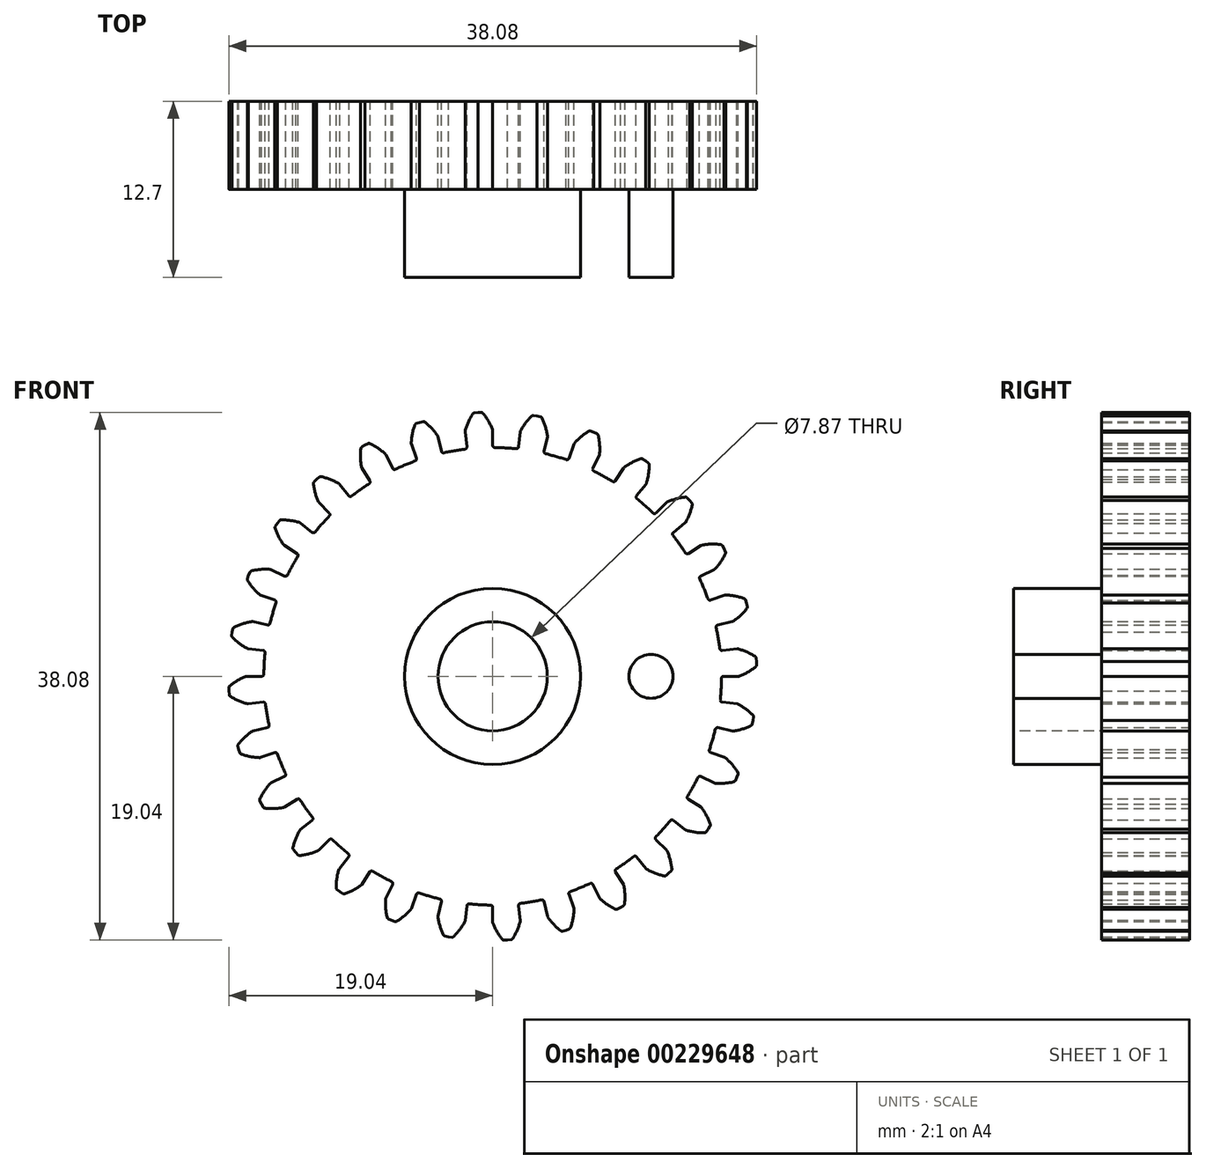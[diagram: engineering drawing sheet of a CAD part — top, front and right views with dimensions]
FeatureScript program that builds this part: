
annotation { "Feature Type Name" : "Feature", "Feature Type Description" : "" }
export const myFeature = defineFeature(function(context is Context, id is Id, definition is map)
    precondition{}
    {
        {
            var Q0;
            Q0=qCreatedBy(makeId("Front.planeOp"),FACE);
            var sketch = newSketch(context, id + "F0", { "sketchPlane" : qUnion([Q0])});
            skArc(sketch, "E0", {"start": v(-2, 16.39) * mm, "mid": v(-2.77, 16.28) * mm, "end": v(-3.53, 16.13) * mm});
            skArc(sketch, "E1.trimOffspring", {"start": v(-0.01, 17.8) * mm, "mid": v(-0.3, 18.42) * mm, "end": v(-0.7, 18.98) * mm});
            skLineSegment(sketch, "E2", {"start": v(-0.81, 19.04) * mm, "end": v(-1.07, 19.04) * mm});
            skLineSegment(sketch, "E3", {"start": v(0, 17.75) * mm, "end": v(0, 16.66) * mm});
            skLineSegment(sketch, "E4.MirrorCS", {"start": v(-1.33, 19) * mm, "end": v(-1.07, 19.04) * mm});
            skArc(sketch, "E5.MirrorCS", {"start": v(-1.98, 17.7) * mm, "mid": v(-1.76, 18.34) * mm, "end": v(-1.44, 18.94) * mm});
            skLineSegment(sketch, "E6.MirrorCS", {"start": v(-1.99, 17.64) * mm, "end": v(-1.87, 16.56) * mm});
            skPoint(sketch, "E7.orphan", {"position": v(0, 16.2) * mm});
            skPoint(sketch, "E8.orphan", {"position": v(-1.81, 16.1) * mm});
            skPoint(sketch, "E9.visualSharp", {"position": v(-1.85, 16.4) * mm});
            skArc(sketch, "E9.filletArc", {"start": v(-2, 16.39) * mm, "mid": v(-1.9, 16.45) * mm, "end": v(-1.87, 16.56) * mm});
            skPoint(sketch, "E10.visualSharp", {"position": v(0, 16.51) * mm});
            skArc(sketch, "E10.filletArc", {"start": v(0, 16.66) * mm, "mid": v(0.04, 16.55) * mm, "end": v(0.15, 16.5) * mm});
            skPoint(sketch, "E11.visualSharp", {"position": v(0, 17.78) * mm});
            skArc(sketch, "E11.filletArc", {"start": v(0, 17.75) * mm, "mid": v(0, 17.78) * mm, "end": v(-0.01, 17.8) * mm});
            skPoint(sketch, "E12.visualSharp", {"position": v(-0.74, 19.04) * mm});
            skArc(sketch, "E12.filletArc", {"start": v(-0.7, 18.98) * mm, "mid": v(-0.75, 19.02) * mm, "end": v(-0.81, 19.04) * mm});
            skPoint(sketch, "E13.visualSharp", {"position": v(-1.4, 19) * mm});
            skArc(sketch, "E13.filletArc", {"start": v(-1.33, 19) * mm, "mid": v(-1.39, 18.98) * mm, "end": v(-1.44, 18.94) * mm});
            skPoint(sketch, "E14.visualSharp", {"position": v(-2, 17.67) * mm});
            skArc(sketch, "E14.filletArc", {"start": v(-1.98, 17.7) * mm, "mid": v(-1.99, 17.67) * mm, "end": v(-1.99, 17.64) * mm});
            skArc(sketch, "E15.1.0", {"start": v(-3.97, 17.36) * mm, "mid": v(-4.4, 17.89) * mm, "end": v(-4.9, 18.35) * mm});
            skPoint(sketch, "E15.1.1", {"position": v(-5.59, 18.21) * mm});
            skPoint(sketch, "E15.1.2", {"position": v(-5.87, 16.78) * mm});
            skLineSegment(sketch, "E15.1.3", {"start": v(-3.95, 17.3) * mm, "end": v(-3.7, 16.24) * mm});
            skLineSegment(sketch, "E15.1.4", {"start": v(-5.86, 16.76) * mm, "end": v(-5.5, 15.73) * mm});
            skArc(sketch, "E15.1.5", {"start": v(-5.87, 16.81) * mm, "mid": v(-5.8, 17.49) * mm, "end": v(-5.62, 18.14) * mm});
            skPoint(sketch, "E15.1.6", {"position": v(-3.96, 17.33) * mm});
            skPoint(sketch, "E15.1.7", {"position": v(-4.96, 18.4) * mm});
            skLineSegment(sketch, "E15.1.8", {"start": v(-5.03, 18.38) * mm, "end": v(-5.28, 18.32) * mm});
            skLineSegment(sketch, "E15.1.9", {"start": v(-5.52, 18.24) * mm, "end": v(-5.28, 18.32) * mm});
            skArc(sketch, "E15.1.10", {"start": v(-5.87, 16.81) * mm, "mid": v(-5.87, 16.78) * mm, "end": v(-5.86, 16.76) * mm});
            skArc(sketch, "E15.1.11", {"start": v(-5.52, 18.24) * mm, "mid": v(-5.58, 18.2) * mm, "end": v(-5.62, 18.14) * mm});
            skArc(sketch, "E15.1.12", {"start": v(-4.9, 18.35) * mm, "mid": v(-4.96, 18.38) * mm, "end": v(-5.03, 18.38) * mm});
            skArc(sketch, "E15.1.13", {"start": v(-3.95, 17.3) * mm, "mid": v(-3.96, 17.33) * mm, "end": v(-3.97, 17.36) * mm});
            skArc(sketch, "E15.1.14", {"start": v(-5.6, 15.53) * mm, "mid": v(-5.5, 15.61) * mm, "end": v(-5.5, 15.73) * mm});
            skArc(sketch, "E15.1.15", {"start": v(-3.7, 16.24) * mm, "mid": v(-3.64, 16.15) * mm, "end": v(-3.53, 16.13) * mm});
            skArc(sketch, "E15.2.0", {"start": v(-7.74, 16.04) * mm, "mid": v(-8.27, 16.46) * mm, "end": v(-8.86, 16.8) * mm});
            skPoint(sketch, "E15.2.1", {"position": v(-9.5, 16.51) * mm});
            skPoint(sketch, "E15.2.2", {"position": v(-9.46, 15.05) * mm});
            skLineSegment(sketch, "E15.2.3", {"start": v(-7.7, 16) * mm, "end": v(-7.23, 15.01) * mm});
            skLineSegment(sketch, "E15.2.4", {"start": v(-9.44, 15.03) * mm, "end": v(-8.86, 14.1) * mm});
            skArc(sketch, "E15.2.5", {"start": v(-9.47, 15.08) * mm, "mid": v(-9.54, 15.76) * mm, "end": v(-9.51, 16.44) * mm});
            skPoint(sketch, "E15.2.6", {"position": v(-7.71, 16.02) * mm});
            skPoint(sketch, "E15.2.7", {"position": v(-8.92, 16.83) * mm});
            skLineSegment(sketch, "E15.2.8", {"start": v(-8.99, 16.8) * mm, "end": v(-9.22, 16.69) * mm});
            skLineSegment(sketch, "E15.2.9", {"start": v(-9.44, 16.55) * mm, "end": v(-9.22, 16.69) * mm});
            skArc(sketch, "E15.2.10", {"start": v(-9.47, 15.08) * mm, "mid": v(-9.46, 15.06) * mm, "end": v(-9.44, 15.03) * mm});
            skArc(sketch, "E15.2.11", {"start": v(-9.44, 16.55) * mm, "mid": v(-9.49, 16.5) * mm, "end": v(-9.51, 16.44) * mm});
            skArc(sketch, "E15.2.12", {"start": v(-8.86, 16.8) * mm, "mid": v(-8.92, 16.81) * mm, "end": v(-8.99, 16.8) * mm});
            skArc(sketch, "E15.2.13", {"start": v(-7.7, 16) * mm, "mid": v(-7.72, 16.02) * mm, "end": v(-7.74, 16.04) * mm});
            skArc(sketch, "E15.2.14", {"start": v(-8.91, 13.9) * mm, "mid": v(-8.84, 14) * mm, "end": v(-8.86, 14.1) * mm});
            skArc(sketch, "E15.2.15", {"start": v(-7.23, 15.01) * mm, "mid": v(-7.14, 14.93) * mm, "end": v(-7.03, 14.94) * mm});
            skArc(sketch, "E16.1.3.0", {"start": v(-11.11, 13.92) * mm, "mid": v(-11.72, 14.2) * mm, "end": v(-12.37, 14.4) * mm});
            skPoint(sketch, "E16.4.3.0", {"position": v(-12.94, 13.98) * mm});
            skPoint(sketch, "E16.5.3.0", {"position": v(-12.57, 12.57) * mm});
            skLineSegment(sketch, "E16.6.3.0", {"start": v(-11.07, 13.88) * mm, "end": v(-10.39, 13.03) * mm});
            skLineSegment(sketch, "E16.9.3.0", {"start": v(-12.55, 12.55) * mm, "end": v(-11.78, 11.78) * mm});
            skArc(sketch, "E16.12.3.0", {"start": v(-12.58, 12.6) * mm, "mid": v(-12.8, 13.24) * mm, "end": v(-12.93, 13.9) * mm});
            skPoint(sketch, "E16.16.3.0", {"position": v(-11.09, 13.9) * mm});
            skPoint(sketch, "E16.17.3.0", {"position": v(-12.45, 14.42) * mm});
            skLineSegment(sketch, "E16.18.3.0", {"start": v(-12.5, 14.38) * mm, "end": v(-12.7, 14.22) * mm});
            skLineSegment(sketch, "E16.21.3.0", {"start": v(-12.89, 14.03) * mm, "end": v(-12.7, 14.22) * mm});
            skArc(sketch, "E16.24.3.0", {"start": v(-12.58, 12.6) * mm, "mid": v(-12.57, 12.57) * mm, "end": v(-12.55, 12.55) * mm});
            skArc(sketch, "E16.28.3.0", {"start": v(-12.89, 14.03) * mm, "mid": v(-12.92, 13.98) * mm, "end": v(-12.93, 13.9) * mm});
            skArc(sketch, "E16.32.3.0", {"start": v(-12.37, 14.4) * mm, "mid": v(-12.44, 14.4) * mm, "end": v(-12.5, 14.38) * mm});
            skArc(sketch, "E16.36.3.0", {"start": v(-11.07, 13.88) * mm, "mid": v(-11.09, 13.9) * mm, "end": v(-11.11, 13.92) * mm});
            skArc(sketch, "E16.40.3.0", {"start": v(-11.78, 11.57) * mm, "mid": v(-11.74, 11.67) * mm, "end": v(-11.78, 11.78) * mm});
            skArc(sketch, "E16.44.3.0", {"start": v(-10.39, 13.03) * mm, "mid": v(-10.29, 12.97) * mm, "end": v(-10.18, 13) * mm});
            skArc(sketch, "E16.1.4.0", {"start": v(-13.93, 11.1) * mm, "mid": v(-14.6, 11.24) * mm, "end": v(-15.27, 11.3) * mm});
            skPoint(sketch, "E16.4.4.0", {"position": v(-15.72, 10.75) * mm});
            skPoint(sketch, "E16.5.4.0", {"position": v(-15.05, 9.46) * mm});
            skLineSegment(sketch, "E16.6.4.0", {"start": v(-13.88, 11.07) * mm, "end": v(-13.03, 10.39) * mm});
            skLineSegment(sketch, "E16.9.4.0", {"start": v(-15.03, 9.44) * mm, "end": v(-14.1, 8.86) * mm});
            skArc(sketch, "E16.12.4.0", {"start": v(-15.07, 9.48) * mm, "mid": v(-15.43, 10.06) * mm, "end": v(-15.7, 10.68) * mm});
            skPoint(sketch, "E16.16.4.0", {"position": v(-13.9, 11.09) * mm});
            skPoint(sketch, "E16.17.4.0", {"position": v(-15.34, 11.3) * mm});
            skLineSegment(sketch, "E16.18.4.0", {"start": v(-15.39, 11.23) * mm, "end": v(-15.55, 11.03) * mm});
            skLineSegment(sketch, "E16.21.4.0", {"start": v(-15.69, 10.81) * mm, "end": v(-15.55, 11.03) * mm});
            skArc(sketch, "E16.24.4.0", {"start": v(-15.07, 9.48) * mm, "mid": v(-15.05, 9.46) * mm, "end": v(-15.03, 9.44) * mm});
            skArc(sketch, "E16.28.4.0", {"start": v(-15.69, 10.81) * mm, "mid": v(-15.7, 10.75) * mm, "end": v(-15.7, 10.68) * mm});
            skArc(sketch, "E16.32.4.0", {"start": v(-15.27, 11.3) * mm, "mid": v(-15.34, 11.28) * mm, "end": v(-15.39, 11.23) * mm});
            skArc(sketch, "E16.36.4.0", {"start": v(-13.88, 11.07) * mm, "mid": v(-13.9, 11.08) * mm, "end": v(-13.93, 11.1) * mm});
            skArc(sketch, "E16.40.4.0", {"start": v(-14.06, 8.66) * mm, "mid": v(-14.04, 8.77) * mm, "end": v(-14.1, 8.86) * mm});
            skArc(sketch, "E16.44.4.0", {"start": v(-13.03, 10.39) * mm, "mid": v(-12.92, 10.36) * mm, "end": v(-12.81, 10.41) * mm});
            skArc(sketch, "E16.1.5.0", {"start": v(-16.05, 7.72) * mm, "mid": v(-16.73, 7.72) * mm, "end": v(-17.4, 7.61) * mm});
            skPoint(sketch, "E16.4.5.0", {"position": v(-17.72, 6.98) * mm});
            skPoint(sketch, "E16.5.5.0", {"position": v(-16.78, 5.87) * mm});
            skLineSegment(sketch, "E16.6.5.0", {"start": v(-16, 7.7) * mm, "end": v(-15.01, 7.23) * mm});
            skLineSegment(sketch, "E16.9.5.0", {"start": v(-16.76, 5.86) * mm, "end": v(-15.73, 5.5) * mm});
            skArc(sketch, "E16.12.5.0", {"start": v(-16.8, 5.9) * mm, "mid": v(-17.28, 6.37) * mm, "end": v(-17.69, 6.92) * mm});
            skPoint(sketch, "E16.16.5.0", {"position": v(-16.02, 7.71) * mm});
            skPoint(sketch, "E16.17.5.0", {"position": v(-17.47, 7.6) * mm});
            skLineSegment(sketch, "E16.18.5.0", {"start": v(-17.5, 7.53) * mm, "end": v(-17.61, 7.3) * mm});
            skLineSegment(sketch, "E16.21.5.0", {"start": v(-17.7, 7.05) * mm, "end": v(-17.61, 7.3) * mm});
            skArc(sketch, "E16.24.5.0", {"start": v(-16.8, 5.9) * mm, "mid": v(-16.78, 5.87) * mm, "end": v(-16.76, 5.86) * mm});
            skArc(sketch, "E16.28.5.0", {"start": v(-17.7, 7.05) * mm, "mid": v(-17.7, 6.99) * mm, "end": v(-17.69, 6.92) * mm});
            skArc(sketch, "E16.32.5.0", {"start": v(-17.4, 7.61) * mm, "mid": v(-17.46, 7.58) * mm, "end": v(-17.5, 7.53) * mm});
            skArc(sketch, "E16.36.5.0", {"start": v(-16, 7.7) * mm, "mid": v(-16.02, 7.71) * mm, "end": v(-16.05, 7.72) * mm});
            skArc(sketch, "E16.40.5.0", {"start": v(-15.63, 5.31) * mm, "mid": v(-15.64, 5.43) * mm, "end": v(-15.73, 5.5) * mm});
            skArc(sketch, "E16.44.5.0", {"start": v(-15.01, 7.23) * mm, "mid": v(-14.9, 7.22) * mm, "end": v(-14.8, 7.3) * mm});
            skArc(sketch, "E16.1.6.0", {"start": v(-17.36, 3.95) * mm, "mid": v(-18.03, 3.8) * mm, "end": v(-18.66, 3.55) * mm});
            skPoint(sketch, "E16.4.6.0", {"position": v(-18.83, 2.87) * mm});
            skPoint(sketch, "E16.5.6.0", {"position": v(-17.67, 2) * mm});
            skLineSegment(sketch, "E16.6.6.0", {"start": v(-17.3, 3.95) * mm, "end": v(-16.24, 3.7) * mm});
            skLineSegment(sketch, "E16.9.6.0", {"start": v(-17.64, 1.99) * mm, "end": v(-16.56, 1.87) * mm});
            skArc(sketch, "E16.12.6.0", {"start": v(-17.7, 2) * mm, "mid": v(-18.27, 2.37) * mm, "end": v(-18.78, 2.81) * mm});
            skPoint(sketch, "E16.16.6.0", {"position": v(-17.33, 3.96) * mm});
            skPoint(sketch, "E16.17.6.0", {"position": v(-18.72, 3.52) * mm});
            skLineSegment(sketch, "E16.18.6.0", {"start": v(-18.74, 3.45) * mm, "end": v(-18.8, 3.2) * mm});
            skLineSegment(sketch, "E16.21.6.0", {"start": v(-18.83, 2.94) * mm, "end": v(-18.8, 3.2) * mm});
            skArc(sketch, "E16.24.6.0", {"start": v(-17.7, 2) * mm, "mid": v(-17.67, 2) * mm, "end": v(-17.64, 1.99) * mm});
            skArc(sketch, "E16.28.6.0", {"start": v(-18.83, 2.94) * mm, "mid": v(-18.82, 2.87) * mm, "end": v(-18.78, 2.81) * mm});
            skArc(sketch, "E16.32.6.0", {"start": v(-18.66, 3.55) * mm, "mid": v(-18.7, 3.5) * mm, "end": v(-18.74, 3.45) * mm});
            skArc(sketch, "E16.36.6.0", {"start": v(-17.3, 3.95) * mm, "mid": v(-17.33, 3.95) * mm, "end": v(-17.36, 3.95) * mm});
            skArc(sketch, "E16.40.6.0", {"start": v(-16.42, 1.7) * mm, "mid": v(-16.46, 1.8) * mm, "end": v(-16.56, 1.87) * mm});
            skArc(sketch, "E16.44.6.0", {"start": v(-16.24, 3.7) * mm, "mid": v(-16.13, 3.73) * mm, "end": v(-16.06, 3.82) * mm});
            skArc(sketch, "E16.1.7.0", {"start": v(-17.8, -0.01) * mm, "mid": v(-18.42, -0.3) * mm, "end": v(-18.98, -0.7) * mm});
            skPoint(sketch, "E16.4.7.0", {"position": v(-19, -1.4) * mm});
            skPoint(sketch, "E16.5.7.0", {"position": v(-17.67, -2) * mm});
            skLineSegment(sketch, "E16.6.7.0", {"start": v(-17.75, 0) * mm, "end": v(-16.66, 0) * mm});
            skLineSegment(sketch, "E16.9.7.0", {"start": v(-17.64, -1.99) * mm, "end": v(-16.56, -1.87) * mm});
            skArc(sketch, "E16.12.7.0", {"start": v(-17.7, -1.98) * mm, "mid": v(-18.34, -1.76) * mm, "end": v(-18.94, -1.44) * mm});
            skPoint(sketch, "E16.16.7.0", {"position": v(-17.78, 0) * mm});
            skPoint(sketch, "E16.17.7.0", {"position": v(-19.04, -0.74) * mm});
            skLineSegment(sketch, "E16.18.7.0", {"start": v(-19.04, -0.81) * mm, "end": v(-19.04, -1.07) * mm});
            skLineSegment(sketch, "E16.21.7.0", {"start": v(-19, -1.33) * mm, "end": v(-19.04, -1.07) * mm});
            skArc(sketch, "E16.24.7.0", {"start": v(-17.7, -1.98) * mm, "mid": v(-17.67, -1.99) * mm, "end": v(-17.64, -1.99) * mm});
            skArc(sketch, "E16.28.7.0", {"start": v(-19, -1.33) * mm, "mid": v(-18.98, -1.39) * mm, "end": v(-18.94, -1.44) * mm});
            skArc(sketch, "E16.32.7.0", {"start": v(-18.98, -0.7) * mm, "mid": v(-19.02, -0.75) * mm, "end": v(-19.04, -0.81) * mm});
            skArc(sketch, "E16.36.7.0", {"start": v(-17.75, 0) * mm, "mid": v(-17.78, 0) * mm, "end": v(-17.8, -0.01) * mm});
            skArc(sketch, "E16.40.7.0", {"start": v(-16.39, -2) * mm, "mid": v(-16.45, -1.9) * mm, "end": v(-16.56, -1.87) * mm});
            skArc(sketch, "E16.44.7.0", {"start": v(-16.66, 0) * mm, "mid": v(-16.55, 0.04) * mm, "end": v(-16.5, 0.15) * mm});
            skArc(sketch, "E16.1.8.0", {"start": v(-17.36, -3.97) * mm, "mid": v(-17.89, -4.4) * mm, "end": v(-18.35, -4.9) * mm});
            skPoint(sketch, "E16.4.8.0", {"position": v(-18.21, -5.59) * mm});
            skPoint(sketch, "E16.5.8.0", {"position": v(-16.78, -5.87) * mm});
            skLineSegment(sketch, "E16.6.8.0", {"start": v(-17.3, -3.95) * mm, "end": v(-16.24, -3.7) * mm});
            skLineSegment(sketch, "E16.9.8.0", {"start": v(-16.76, -5.86) * mm, "end": v(-15.73, -5.5) * mm});
            skArc(sketch, "E16.12.8.0", {"start": v(-16.81, -5.87) * mm, "mid": v(-17.49, -5.8) * mm, "end": v(-18.14, -5.62) * mm});
            skPoint(sketch, "E16.16.8.0", {"position": v(-17.33, -3.96) * mm});
            skPoint(sketch, "E16.17.8.0", {"position": v(-18.4, -4.96) * mm});
            skLineSegment(sketch, "E16.18.8.0", {"start": v(-18.38, -5.03) * mm, "end": v(-18.32, -5.28) * mm});
            skLineSegment(sketch, "E16.21.8.0", {"start": v(-18.24, -5.52) * mm, "end": v(-18.32, -5.28) * mm});
            skArc(sketch, "E16.24.8.0", {"start": v(-16.81, -5.87) * mm, "mid": v(-16.78, -5.87) * mm, "end": v(-16.76, -5.86) * mm});
            skArc(sketch, "E16.28.8.0", {"start": v(-18.24, -5.52) * mm, "mid": v(-18.2, -5.58) * mm, "end": v(-18.14, -5.62) * mm});
            skArc(sketch, "E16.32.8.0", {"start": v(-18.35, -4.9) * mm, "mid": v(-18.38, -4.96) * mm, "end": v(-18.38, -5.03) * mm});
            skArc(sketch, "E16.36.8.0", {"start": v(-17.3, -3.95) * mm, "mid": v(-17.33, -3.96) * mm, "end": v(-17.36, -3.97) * mm});
            skArc(sketch, "E16.40.8.0", {"start": v(-15.53, -5.6) * mm, "mid": v(-15.61, -5.5) * mm, "end": v(-15.73, -5.5) * mm});
            skArc(sketch, "E16.44.8.0", {"start": v(-16.24, -3.7) * mm, "mid": v(-16.15, -3.64) * mm, "end": v(-16.13, -3.53) * mm});
            skArc(sketch, "E16.1.9.0", {"start": v(-16.04, -7.74) * mm, "mid": v(-16.46, -8.27) * mm, "end": v(-16.8, -8.86) * mm});
            skPoint(sketch, "E16.4.9.0", {"position": v(-16.51, -9.5) * mm});
            skPoint(sketch, "E16.5.9.0", {"position": v(-15.05, -9.46) * mm});
            skLineSegment(sketch, "E16.6.9.0", {"start": v(-16, -7.7) * mm, "end": v(-15.01, -7.23) * mm});
            skLineSegment(sketch, "E16.9.9.0", {"start": v(-15.03, -9.44) * mm, "end": v(-14.1, -8.86) * mm});
            skArc(sketch, "E16.12.9.0", {"start": v(-15.08, -9.47) * mm, "mid": v(-15.76, -9.54) * mm, "end": v(-16.44, -9.51) * mm});
            skPoint(sketch, "E16.16.9.0", {"position": v(-16.02, -7.71) * mm});
            skPoint(sketch, "E16.17.9.0", {"position": v(-16.83, -8.92) * mm});
            skLineSegment(sketch, "E16.18.9.0", {"start": v(-16.8, -8.99) * mm, "end": v(-16.69, -9.22) * mm});
            skLineSegment(sketch, "E16.21.9.0", {"start": v(-16.55, -9.44) * mm, "end": v(-16.69, -9.22) * mm});
            skArc(sketch, "E16.24.9.0", {"start": v(-15.08, -9.47) * mm, "mid": v(-15.06, -9.46) * mm, "end": v(-15.03, -9.44) * mm});
            skArc(sketch, "E16.28.9.0", {"start": v(-16.55, -9.44) * mm, "mid": v(-16.5, -9.49) * mm, "end": v(-16.44, -9.51) * mm});
            skArc(sketch, "E16.32.9.0", {"start": v(-16.8, -8.86) * mm, "mid": v(-16.81, -8.92) * mm, "end": v(-16.8, -8.99) * mm});
            skArc(sketch, "E16.36.9.0", {"start": v(-16, -7.7) * mm, "mid": v(-16.02, -7.72) * mm, "end": v(-16.04, -7.74) * mm});
            skArc(sketch, "E16.40.9.0", {"start": v(-13.9, -8.91) * mm, "mid": v(-14, -8.84) * mm, "end": v(-14.1, -8.86) * mm});
            skArc(sketch, "E16.44.9.0", {"start": v(-15.01, -7.23) * mm, "mid": v(-14.93, -7.14) * mm, "end": v(-14.94, -7.03) * mm});
            skArc(sketch, "E16.1.10.0", {"start": v(-13.92, -11.11) * mm, "mid": v(-14.2, -11.72) * mm, "end": v(-14.4, -12.37) * mm});
            skPoint(sketch, "E16.4.10.0", {"position": v(-13.98, -12.94) * mm});
            skPoint(sketch, "E16.5.10.0", {"position": v(-12.57, -12.57) * mm});
            skLineSegment(sketch, "E16.6.10.0", {"start": v(-13.88, -11.07) * mm, "end": v(-13.03, -10.39) * mm});
            skLineSegment(sketch, "E16.9.10.0", {"start": v(-12.55, -12.55) * mm, "end": v(-11.78, -11.78) * mm});
            skArc(sketch, "E16.12.10.0", {"start": v(-12.6, -12.58) * mm, "mid": v(-13.24, -12.8) * mm, "end": v(-13.9, -12.93) * mm});
            skPoint(sketch, "E16.16.10.0", {"position": v(-13.9, -11.09) * mm});
            skPoint(sketch, "E16.17.10.0", {"position": v(-14.42, -12.45) * mm});
            skLineSegment(sketch, "E16.18.10.0", {"start": v(-14.38, -12.5) * mm, "end": v(-14.22, -12.7) * mm});
            skLineSegment(sketch, "E16.21.10.0", {"start": v(-14.03, -12.89) * mm, "end": v(-14.22, -12.7) * mm});
            skArc(sketch, "E16.24.10.0", {"start": v(-12.6, -12.58) * mm, "mid": v(-12.57, -12.57) * mm, "end": v(-12.55, -12.55) * mm});
            skArc(sketch, "E16.28.10.0", {"start": v(-14.03, -12.89) * mm, "mid": v(-13.98, -12.92) * mm, "end": v(-13.9, -12.93) * mm});
            skArc(sketch, "E16.32.10.0", {"start": v(-14.4, -12.37) * mm, "mid": v(-14.4, -12.44) * mm, "end": v(-14.38, -12.5) * mm});
            skArc(sketch, "E16.36.10.0", {"start": v(-13.88, -11.07) * mm, "mid": v(-13.9, -11.09) * mm, "end": v(-13.92, -11.11) * mm});
            skArc(sketch, "E16.40.10.0", {"start": v(-11.57, -11.78) * mm, "mid": v(-11.67, -11.74) * mm, "end": v(-11.78, -11.78) * mm});
            skArc(sketch, "E16.44.10.0", {"start": v(-13.03, -10.39) * mm, "mid": v(-12.97, -10.29) * mm, "end": v(-13, -10.18) * mm});
            skArc(sketch, "E16.1.11.0", {"start": v(-11.1, -13.93) * mm, "mid": v(-11.24, -14.6) * mm, "end": v(-11.3, -15.27) * mm});
            skPoint(sketch, "E16.4.11.0", {"position": v(-10.75, -15.72) * mm});
            skPoint(sketch, "E16.5.11.0", {"position": v(-9.46, -15.05) * mm});
            skLineSegment(sketch, "E16.6.11.0", {"start": v(-11.07, -13.88) * mm, "end": v(-10.39, -13.03) * mm});
            skLineSegment(sketch, "E16.9.11.0", {"start": v(-9.44, -15.03) * mm, "end": v(-8.86, -14.1) * mm});
            skArc(sketch, "E16.12.11.0", {"start": v(-9.48, -15.07) * mm, "mid": v(-10.06, -15.43) * mm, "end": v(-10.68, -15.7) * mm});
            skPoint(sketch, "E16.16.11.0", {"position": v(-11.09, -13.9) * mm});
            skPoint(sketch, "E16.17.11.0", {"position": v(-11.3, -15.34) * mm});
            skLineSegment(sketch, "E16.18.11.0", {"start": v(-11.23, -15.39) * mm, "end": v(-11.03, -15.55) * mm});
            skLineSegment(sketch, "E16.21.11.0", {"start": v(-10.81, -15.69) * mm, "end": v(-11.03, -15.55) * mm});
            skArc(sketch, "E16.24.11.0", {"start": v(-9.48, -15.07) * mm, "mid": v(-9.46, -15.05) * mm, "end": v(-9.44, -15.03) * mm});
            skArc(sketch, "E16.28.11.0", {"start": v(-10.81, -15.69) * mm, "mid": v(-10.75, -15.7) * mm, "end": v(-10.68, -15.7) * mm});
            skArc(sketch, "E16.32.11.0", {"start": v(-11.3, -15.27) * mm, "mid": v(-11.28, -15.34) * mm, "end": v(-11.23, -15.39) * mm});
            skArc(sketch, "E16.36.11.0", {"start": v(-11.07, -13.88) * mm, "mid": v(-11.08, -13.9) * mm, "end": v(-11.1, -13.93) * mm});
            skArc(sketch, "E16.40.11.0", {"start": v(-8.66, -14.06) * mm, "mid": v(-8.77, -14.04) * mm, "end": v(-8.86, -14.1) * mm});
            skArc(sketch, "E16.44.11.0", {"start": v(-10.39, -13.03) * mm, "mid": v(-10.36, -12.92) * mm, "end": v(-10.41, -12.81) * mm});
            skArc(sketch, "E16.1.12.0", {"start": v(-7.72, -16.05) * mm, "mid": v(-7.72, -16.73) * mm, "end": v(-7.61, -17.4) * mm});
            skPoint(sketch, "E16.4.12.0", {"position": v(-6.98, -17.72) * mm});
            skPoint(sketch, "E16.5.12.0", {"position": v(-5.87, -16.78) * mm});
            skLineSegment(sketch, "E16.6.12.0", {"start": v(-7.7, -16) * mm, "end": v(-7.23, -15.01) * mm});
            skLineSegment(sketch, "E16.9.12.0", {"start": v(-5.86, -16.76) * mm, "end": v(-5.5, -15.73) * mm});
            skArc(sketch, "E16.12.12.0", {"start": v(-5.9, -16.8) * mm, "mid": v(-6.37, -17.28) * mm, "end": v(-6.92, -17.69) * mm});
            skPoint(sketch, "E16.16.12.0", {"position": v(-7.71, -16.02) * mm});
            skPoint(sketch, "E16.17.12.0", {"position": v(-7.6, -17.47) * mm});
            skLineSegment(sketch, "E16.18.12.0", {"start": v(-7.53, -17.5) * mm, "end": v(-7.3, -17.61) * mm});
            skLineSegment(sketch, "E16.21.12.0", {"start": v(-7.05, -17.7) * mm, "end": v(-7.3, -17.61) * mm});
            skArc(sketch, "E16.24.12.0", {"start": v(-5.9, -16.8) * mm, "mid": v(-5.87, -16.78) * mm, "end": v(-5.86, -16.76) * mm});
            skArc(sketch, "E16.28.12.0", {"start": v(-7.05, -17.7) * mm, "mid": v(-6.99, -17.7) * mm, "end": v(-6.92, -17.69) * mm});
            skArc(sketch, "E16.32.12.0", {"start": v(-7.61, -17.4) * mm, "mid": v(-7.58, -17.46) * mm, "end": v(-7.53, -17.5) * mm});
            skArc(sketch, "E16.36.12.0", {"start": v(-7.7, -16) * mm, "mid": v(-7.71, -16.02) * mm, "end": v(-7.72, -16.05) * mm});
            skArc(sketch, "E16.40.12.0", {"start": v(-5.31, -15.63) * mm, "mid": v(-5.43, -15.64) * mm, "end": v(-5.5, -15.73) * mm});
            skArc(sketch, "E16.44.12.0", {"start": v(-7.23, -15.01) * mm, "mid": v(-7.22, -14.9) * mm, "end": v(-7.3, -14.8) * mm});
            skArc(sketch, "E16.1.13.0", {"start": v(-3.95, -17.36) * mm, "mid": v(-3.8, -18.03) * mm, "end": v(-3.55, -18.66) * mm});
            skPoint(sketch, "E16.4.13.0", {"position": v(-2.87, -18.83) * mm});
            skPoint(sketch, "E16.5.13.0", {"position": v(-2, -17.67) * mm});
            skLineSegment(sketch, "E16.6.13.0", {"start": v(-3.95, -17.3) * mm, "end": v(-3.7, -16.24) * mm});
            skLineSegment(sketch, "E16.9.13.0", {"start": v(-1.99, -17.64) * mm, "end": v(-1.87, -16.56) * mm});
            skArc(sketch, "E16.12.13.0", {"start": v(-2, -17.7) * mm, "mid": v(-2.37, -18.27) * mm, "end": v(-2.81, -18.78) * mm});
            skPoint(sketch, "E16.16.13.0", {"position": v(-3.96, -17.33) * mm});
            skPoint(sketch, "E16.17.13.0", {"position": v(-3.52, -18.72) * mm});
            skLineSegment(sketch, "E16.18.13.0", {"start": v(-3.45, -18.74) * mm, "end": v(-3.2, -18.8) * mm});
            skLineSegment(sketch, "E16.21.13.0", {"start": v(-2.94, -18.83) * mm, "end": v(-3.2, -18.8) * mm});
            skArc(sketch, "E16.24.13.0", {"start": v(-2, -17.7) * mm, "mid": v(-2, -17.67) * mm, "end": v(-1.99, -17.64) * mm});
            skArc(sketch, "E16.28.13.0", {"start": v(-2.94, -18.83) * mm, "mid": v(-2.87, -18.82) * mm, "end": v(-2.81, -18.78) * mm});
            skArc(sketch, "E16.32.13.0", {"start": v(-3.55, -18.66) * mm, "mid": v(-3.5, -18.7) * mm, "end": v(-3.45, -18.74) * mm});
            skArc(sketch, "E16.36.13.0", {"start": v(-3.95, -17.3) * mm, "mid": v(-3.95, -17.33) * mm, "end": v(-3.95, -17.36) * mm});
            skArc(sketch, "E16.40.13.0", {"start": v(-1.7, -16.42) * mm, "mid": v(-1.8, -16.46) * mm, "end": v(-1.87, -16.56) * mm});
            skArc(sketch, "E16.44.13.0", {"start": v(-3.7, -16.24) * mm, "mid": v(-3.73, -16.13) * mm, "end": v(-3.82, -16.06) * mm});
            skArc(sketch, "E16.1.14.0", {"start": v(0.01, -17.8) * mm, "mid": v(0.3, -18.42) * mm, "end": v(0.7, -18.98) * mm});
            skPoint(sketch, "E16.4.14.0", {"position": v(1.4, -19) * mm});
            skPoint(sketch, "E16.5.14.0", {"position": v(2, -17.67) * mm});
            skLineSegment(sketch, "E16.6.14.0", {"start": v(0, -17.75) * mm, "end": v(0, -16.66) * mm});
            skLineSegment(sketch, "E16.9.14.0", {"start": v(1.99, -17.64) * mm, "end": v(1.87, -16.56) * mm});
            skArc(sketch, "E16.12.14.0", {"start": v(1.98, -17.7) * mm, "mid": v(1.76, -18.34) * mm, "end": v(1.44, -18.94) * mm});
            skPoint(sketch, "E16.16.14.0", {"position": v(0, -17.78) * mm});
            skPoint(sketch, "E16.17.14.0", {"position": v(0.74, -19.04) * mm});
            skLineSegment(sketch, "E16.18.14.0", {"start": v(0.81, -19.04) * mm, "end": v(1.07, -19.04) * mm});
            skLineSegment(sketch, "E16.21.14.0", {"start": v(1.33, -19) * mm, "end": v(1.07, -19.04) * mm});
            skArc(sketch, "E16.24.14.0", {"start": v(1.98, -17.7) * mm, "mid": v(1.99, -17.67) * mm, "end": v(1.99, -17.64) * mm});
            skArc(sketch, "E16.28.14.0", {"start": v(1.33, -19) * mm, "mid": v(1.39, -18.98) * mm, "end": v(1.44, -18.94) * mm});
            skArc(sketch, "E16.32.14.0", {"start": v(0.7, -18.98) * mm, "mid": v(0.75, -19.02) * mm, "end": v(0.81, -19.04) * mm});
            skArc(sketch, "E16.36.14.0", {"start": v(0, -17.75) * mm, "mid": v(0, -17.78) * mm, "end": v(0.01, -17.8) * mm});
            skArc(sketch, "E16.40.14.0", {"start": v(2, -16.39) * mm, "mid": v(1.9, -16.45) * mm, "end": v(1.87, -16.56) * mm});
            skArc(sketch, "E16.44.14.0", {"start": v(0, -16.66) * mm, "mid": v(-0.04, -16.55) * mm, "end": v(-0.15, -16.5) * mm});
            skArc(sketch, "E16.1.15.0", {"start": v(3.97, -17.36) * mm, "mid": v(4.4, -17.89) * mm, "end": v(4.9, -18.35) * mm});
            skPoint(sketch, "E16.4.15.0", {"position": v(5.59, -18.21) * mm});
            skPoint(sketch, "E16.5.15.0", {"position": v(5.87, -16.78) * mm});
            skLineSegment(sketch, "E16.6.15.0", {"start": v(3.95, -17.3) * mm, "end": v(3.7, -16.24) * mm});
            skLineSegment(sketch, "E16.9.15.0", {"start": v(5.86, -16.76) * mm, "end": v(5.5, -15.73) * mm});
            skArc(sketch, "E16.12.15.0", {"start": v(5.87, -16.81) * mm, "mid": v(5.8, -17.49) * mm, "end": v(5.62, -18.14) * mm});
            skPoint(sketch, "E16.16.15.0", {"position": v(3.96, -17.33) * mm});
            skPoint(sketch, "E16.17.15.0", {"position": v(4.96, -18.4) * mm});
            skLineSegment(sketch, "E16.18.15.0", {"start": v(5.03, -18.38) * mm, "end": v(5.28, -18.32) * mm});
            skLineSegment(sketch, "E16.21.15.0", {"start": v(5.52, -18.24) * mm, "end": v(5.28, -18.32) * mm});
            skArc(sketch, "E16.24.15.0", {"start": v(5.87, -16.81) * mm, "mid": v(5.87, -16.78) * mm, "end": v(5.86, -16.76) * mm});
            skArc(sketch, "E16.28.15.0", {"start": v(5.52, -18.24) * mm, "mid": v(5.58, -18.2) * mm, "end": v(5.62, -18.14) * mm});
            skArc(sketch, "E16.32.15.0", {"start": v(4.9, -18.35) * mm, "mid": v(4.96, -18.38) * mm, "end": v(5.03, -18.38) * mm});
            skArc(sketch, "E16.36.15.0", {"start": v(3.95, -17.3) * mm, "mid": v(3.96, -17.33) * mm, "end": v(3.97, -17.36) * mm});
            skArc(sketch, "E16.40.15.0", {"start": v(5.6, -15.53) * mm, "mid": v(5.5, -15.61) * mm, "end": v(5.5, -15.73) * mm});
            skArc(sketch, "E16.44.15.0", {"start": v(3.7, -16.24) * mm, "mid": v(3.64, -16.15) * mm, "end": v(3.53, -16.13) * mm});
            skArc(sketch, "E16.1.16.0", {"start": v(7.74, -16.04) * mm, "mid": v(8.27, -16.46) * mm, "end": v(8.86, -16.8) * mm});
            skPoint(sketch, "E16.4.16.0", {"position": v(9.5, -16.51) * mm});
            skPoint(sketch, "E16.5.16.0", {"position": v(9.46, -15.05) * mm});
            skLineSegment(sketch, "E16.6.16.0", {"start": v(7.7, -16) * mm, "end": v(7.23, -15.01) * mm});
            skLineSegment(sketch, "E16.9.16.0", {"start": v(9.44, -15.03) * mm, "end": v(8.86, -14.1) * mm});
            skArc(sketch, "E16.12.16.0", {"start": v(9.47, -15.08) * mm, "mid": v(9.54, -15.76) * mm, "end": v(9.51, -16.44) * mm});
            skPoint(sketch, "E16.16.16.0", {"position": v(7.71, -16.02) * mm});
            skPoint(sketch, "E16.17.16.0", {"position": v(8.92, -16.83) * mm});
            skLineSegment(sketch, "E16.18.16.0", {"start": v(8.99, -16.8) * mm, "end": v(9.22, -16.69) * mm});
            skLineSegment(sketch, "E16.21.16.0", {"start": v(9.44, -16.55) * mm, "end": v(9.22, -16.69) * mm});
            skArc(sketch, "E16.24.16.0", {"start": v(9.47, -15.08) * mm, "mid": v(9.46, -15.06) * mm, "end": v(9.44, -15.03) * mm});
            skArc(sketch, "E16.28.16.0", {"start": v(9.44, -16.55) * mm, "mid": v(9.49, -16.5) * mm, "end": v(9.51, -16.44) * mm});
            skArc(sketch, "E16.32.16.0", {"start": v(8.86, -16.8) * mm, "mid": v(8.92, -16.81) * mm, "end": v(8.99, -16.8) * mm});
            skArc(sketch, "E16.36.16.0", {"start": v(7.7, -16) * mm, "mid": v(7.72, -16.02) * mm, "end": v(7.74, -16.04) * mm});
            skArc(sketch, "E16.40.16.0", {"start": v(8.91, -13.9) * mm, "mid": v(8.84, -14) * mm, "end": v(8.86, -14.1) * mm});
            skArc(sketch, "E16.44.16.0", {"start": v(7.23, -15.01) * mm, "mid": v(7.14, -14.93) * mm, "end": v(7.03, -14.94) * mm});
            skArc(sketch, "E16.1.17.0", {"start": v(11.11, -13.92) * mm, "mid": v(11.72, -14.2) * mm, "end": v(12.37, -14.4) * mm});
            skPoint(sketch, "E16.4.17.0", {"position": v(12.94, -13.98) * mm});
            skPoint(sketch, "E16.5.17.0", {"position": v(12.57, -12.57) * mm});
            skLineSegment(sketch, "E16.6.17.0", {"start": v(11.07, -13.88) * mm, "end": v(10.39, -13.03) * mm});
            skLineSegment(sketch, "E16.9.17.0", {"start": v(12.55, -12.55) * mm, "end": v(11.78, -11.78) * mm});
            skArc(sketch, "E16.12.17.0", {"start": v(12.58, -12.6) * mm, "mid": v(12.8, -13.24) * mm, "end": v(12.93, -13.9) * mm});
            skPoint(sketch, "E16.16.17.0", {"position": v(11.09, -13.9) * mm});
            skPoint(sketch, "E16.17.17.0", {"position": v(12.45, -14.42) * mm});
            skLineSegment(sketch, "E16.18.17.0", {"start": v(12.5, -14.38) * mm, "end": v(12.7, -14.22) * mm});
            skLineSegment(sketch, "E16.21.17.0", {"start": v(12.89, -14.03) * mm, "end": v(12.7, -14.22) * mm});
            skArc(sketch, "E16.24.17.0", {"start": v(12.58, -12.6) * mm, "mid": v(12.57, -12.57) * mm, "end": v(12.55, -12.55) * mm});
            skArc(sketch, "E16.28.17.0", {"start": v(12.89, -14.03) * mm, "mid": v(12.92, -13.98) * mm, "end": v(12.93, -13.9) * mm});
            skArc(sketch, "E16.32.17.0", {"start": v(12.37, -14.4) * mm, "mid": v(12.44, -14.4) * mm, "end": v(12.5, -14.38) * mm});
            skArc(sketch, "E16.36.17.0", {"start": v(11.07, -13.88) * mm, "mid": v(11.09, -13.9) * mm, "end": v(11.11, -13.92) * mm});
            skArc(sketch, "E16.40.17.0", {"start": v(11.78, -11.57) * mm, "mid": v(11.74, -11.67) * mm, "end": v(11.78, -11.78) * mm});
            skArc(sketch, "E16.44.17.0", {"start": v(10.39, -13.03) * mm, "mid": v(10.29, -12.97) * mm, "end": v(10.18, -13) * mm});
            skArc(sketch, "E16.1.18.0", {"start": v(13.93, -11.1) * mm, "mid": v(14.6, -11.24) * mm, "end": v(15.27, -11.3) * mm});
            skPoint(sketch, "E16.4.18.0", {"position": v(15.72, -10.75) * mm});
            skPoint(sketch, "E16.5.18.0", {"position": v(15.05, -9.46) * mm});
            skLineSegment(sketch, "E16.6.18.0", {"start": v(13.88, -11.07) * mm, "end": v(13.03, -10.39) * mm});
            skLineSegment(sketch, "E16.9.18.0", {"start": v(15.03, -9.44) * mm, "end": v(14.1, -8.86) * mm});
            skArc(sketch, "E16.12.18.0", {"start": v(15.07, -9.48) * mm, "mid": v(15.43, -10.06) * mm, "end": v(15.7, -10.68) * mm});
            skPoint(sketch, "E16.16.18.0", {"position": v(13.9, -11.09) * mm});
            skPoint(sketch, "E16.17.18.0", {"position": v(15.34, -11.3) * mm});
            skLineSegment(sketch, "E16.18.18.0", {"start": v(15.39, -11.23) * mm, "end": v(15.55, -11.03) * mm});
            skLineSegment(sketch, "E16.21.18.0", {"start": v(15.69, -10.81) * mm, "end": v(15.55, -11.03) * mm});
            skArc(sketch, "E16.24.18.0", {"start": v(15.07, -9.48) * mm, "mid": v(15.05, -9.46) * mm, "end": v(15.03, -9.44) * mm});
            skArc(sketch, "E16.28.18.0", {"start": v(15.69, -10.81) * mm, "mid": v(15.7, -10.75) * mm, "end": v(15.7, -10.68) * mm});
            skArc(sketch, "E16.32.18.0", {"start": v(15.27, -11.3) * mm, "mid": v(15.34, -11.28) * mm, "end": v(15.39, -11.23) * mm});
            skArc(sketch, "E16.36.18.0", {"start": v(13.88, -11.07) * mm, "mid": v(13.9, -11.08) * mm, "end": v(13.93, -11.1) * mm});
            skArc(sketch, "E16.40.18.0", {"start": v(14.06, -8.66) * mm, "mid": v(14.04, -8.77) * mm, "end": v(14.1, -8.86) * mm});
            skArc(sketch, "E16.44.18.0", {"start": v(13.03, -10.39) * mm, "mid": v(12.92, -10.36) * mm, "end": v(12.81, -10.41) * mm});
            skArc(sketch, "E16.1.19.0", {"start": v(16.05, -7.72) * mm, "mid": v(16.73, -7.72) * mm, "end": v(17.4, -7.61) * mm});
            skPoint(sketch, "E16.4.19.0", {"position": v(17.72, -6.98) * mm});
            skPoint(sketch, "E16.5.19.0", {"position": v(16.78, -5.87) * mm});
            skLineSegment(sketch, "E16.6.19.0", {"start": v(16, -7.7) * mm, "end": v(15.01, -7.23) * mm});
            skLineSegment(sketch, "E16.9.19.0", {"start": v(16.76, -5.86) * mm, "end": v(15.73, -5.5) * mm});
            skArc(sketch, "E16.12.19.0", {"start": v(16.8, -5.9) * mm, "mid": v(17.28, -6.37) * mm, "end": v(17.69, -6.92) * mm});
            skPoint(sketch, "E16.16.19.0", {"position": v(16.02, -7.71) * mm});
            skPoint(sketch, "E16.17.19.0", {"position": v(17.47, -7.6) * mm});
            skLineSegment(sketch, "E16.18.19.0", {"start": v(17.5, -7.53) * mm, "end": v(17.61, -7.3) * mm});
            skLineSegment(sketch, "E16.21.19.0", {"start": v(17.7, -7.05) * mm, "end": v(17.61, -7.3) * mm});
            skArc(sketch, "E16.24.19.0", {"start": v(16.8, -5.9) * mm, "mid": v(16.78, -5.87) * mm, "end": v(16.76, -5.86) * mm});
            skArc(sketch, "E16.28.19.0", {"start": v(17.7, -7.05) * mm, "mid": v(17.7, -6.99) * mm, "end": v(17.69, -6.92) * mm});
            skArc(sketch, "E16.32.19.0", {"start": v(17.4, -7.61) * mm, "mid": v(17.46, -7.58) * mm, "end": v(17.5, -7.53) * mm});
            skArc(sketch, "E16.36.19.0", {"start": v(16, -7.7) * mm, "mid": v(16.02, -7.71) * mm, "end": v(16.05, -7.72) * mm});
            skArc(sketch, "E16.40.19.0", {"start": v(15.63, -5.31) * mm, "mid": v(15.64, -5.43) * mm, "end": v(15.73, -5.5) * mm});
            skArc(sketch, "E16.44.19.0", {"start": v(15.01, -7.23) * mm, "mid": v(14.9, -7.22) * mm, "end": v(14.8, -7.3) * mm});
            skArc(sketch, "E16.1.20.0", {"start": v(17.36, -3.95) * mm, "mid": v(18.03, -3.8) * mm, "end": v(18.66, -3.55) * mm});
            skPoint(sketch, "E16.4.20.0", {"position": v(18.83, -2.87) * mm});
            skPoint(sketch, "E16.5.20.0", {"position": v(17.67, -2) * mm});
            skLineSegment(sketch, "E16.6.20.0", {"start": v(17.3, -3.95) * mm, "end": v(16.24, -3.7) * mm});
            skLineSegment(sketch, "E16.9.20.0", {"start": v(17.64, -1.99) * mm, "end": v(16.56, -1.87) * mm});
            skArc(sketch, "E16.12.20.0", {"start": v(17.7, -2) * mm, "mid": v(18.27, -2.37) * mm, "end": v(18.78, -2.81) * mm});
            skPoint(sketch, "E16.16.20.0", {"position": v(17.33, -3.96) * mm});
            skPoint(sketch, "E16.17.20.0", {"position": v(18.72, -3.52) * mm});
            skLineSegment(sketch, "E16.18.20.0", {"start": v(18.74, -3.45) * mm, "end": v(18.8, -3.2) * mm});
            skLineSegment(sketch, "E16.21.20.0", {"start": v(18.83, -2.94) * mm, "end": v(18.8, -3.2) * mm});
            skArc(sketch, "E16.24.20.0", {"start": v(17.7, -2) * mm, "mid": v(17.67, -2) * mm, "end": v(17.64, -1.99) * mm});
            skArc(sketch, "E16.28.20.0", {"start": v(18.83, -2.94) * mm, "mid": v(18.82, -2.87) * mm, "end": v(18.78, -2.81) * mm});
            skArc(sketch, "E16.32.20.0", {"start": v(18.66, -3.55) * mm, "mid": v(18.7, -3.5) * mm, "end": v(18.74, -3.45) * mm});
            skArc(sketch, "E16.36.20.0", {"start": v(17.3, -3.95) * mm, "mid": v(17.33, -3.95) * mm, "end": v(17.36, -3.95) * mm});
            skArc(sketch, "E16.40.20.0", {"start": v(16.42, -1.7) * mm, "mid": v(16.46, -1.8) * mm, "end": v(16.56, -1.87) * mm});
            skArc(sketch, "E16.44.20.0", {"start": v(16.24, -3.7) * mm, "mid": v(16.13, -3.73) * mm, "end": v(16.06, -3.82) * mm});
            skArc(sketch, "E16.1.21.0", {"start": v(17.8, 0.01) * mm, "mid": v(18.42, 0.3) * mm, "end": v(18.98, 0.7) * mm});
            skPoint(sketch, "E16.4.21.0", {"position": v(19, 1.4) * mm});
            skPoint(sketch, "E16.5.21.0", {"position": v(17.67, 2) * mm});
            skLineSegment(sketch, "E16.6.21.0", {"start": v(17.75, 0) * mm, "end": v(16.66, 0) * mm});
            skLineSegment(sketch, "E16.9.21.0", {"start": v(17.64, 1.99) * mm, "end": v(16.56, 1.87) * mm});
            skArc(sketch, "E16.12.21.0", {"start": v(17.7, 1.98) * mm, "mid": v(18.34, 1.76) * mm, "end": v(18.94, 1.44) * mm});
            skPoint(sketch, "E16.16.21.0", {"position": v(17.78, 0) * mm});
            skPoint(sketch, "E16.17.21.0", {"position": v(19.04, 0.74) * mm});
            skLineSegment(sketch, "E16.18.21.0", {"start": v(19.04, 0.81) * mm, "end": v(19.04, 1.07) * mm});
            skLineSegment(sketch, "E16.21.21.0", {"start": v(19, 1.33) * mm, "end": v(19.04, 1.07) * mm});
            skArc(sketch, "E16.24.21.0", {"start": v(17.7, 1.98) * mm, "mid": v(17.67, 1.99) * mm, "end": v(17.64, 1.99) * mm});
            skArc(sketch, "E16.28.21.0", {"start": v(19, 1.33) * mm, "mid": v(18.98, 1.39) * mm, "end": v(18.94, 1.44) * mm});
            skArc(sketch, "E16.32.21.0", {"start": v(18.98, 0.7) * mm, "mid": v(19.02, 0.75) * mm, "end": v(19.04, 0.81) * mm});
            skArc(sketch, "E16.36.21.0", {"start": v(17.75, 0) * mm, "mid": v(17.78, 0) * mm, "end": v(17.8, 0.01) * mm});
            skArc(sketch, "E16.40.21.0", {"start": v(16.39, 2) * mm, "mid": v(16.45, 1.9) * mm, "end": v(16.56, 1.87) * mm});
            skArc(sketch, "E16.44.21.0", {"start": v(16.66, 0) * mm, "mid": v(16.55, -0.04) * mm, "end": v(16.5, -0.15) * mm});
            skArc(sketch, "E16.1.22.0", {"start": v(17.36, 3.97) * mm, "mid": v(17.89, 4.4) * mm, "end": v(18.35, 4.9) * mm});
            skPoint(sketch, "E16.4.22.0", {"position": v(18.21, 5.59) * mm});
            skPoint(sketch, "E16.5.22.0", {"position": v(16.78, 5.87) * mm});
            skLineSegment(sketch, "E16.6.22.0", {"start": v(17.3, 3.95) * mm, "end": v(16.24, 3.7) * mm});
            skLineSegment(sketch, "E16.9.22.0", {"start": v(16.76, 5.86) * mm, "end": v(15.73, 5.5) * mm});
            skArc(sketch, "E16.12.22.0", {"start": v(16.81, 5.87) * mm, "mid": v(17.49, 5.8) * mm, "end": v(18.14, 5.62) * mm});
            skPoint(sketch, "E16.16.22.0", {"position": v(17.33, 3.96) * mm});
            skPoint(sketch, "E16.17.22.0", {"position": v(18.4, 4.96) * mm});
            skLineSegment(sketch, "E16.18.22.0", {"start": v(18.38, 5.03) * mm, "end": v(18.32, 5.28) * mm});
            skLineSegment(sketch, "E16.21.22.0", {"start": v(18.24, 5.52) * mm, "end": v(18.32, 5.28) * mm});
            skArc(sketch, "E16.24.22.0", {"start": v(16.81, 5.87) * mm, "mid": v(16.78, 5.87) * mm, "end": v(16.76, 5.86) * mm});
            skArc(sketch, "E16.28.22.0", {"start": v(18.24, 5.52) * mm, "mid": v(18.2, 5.58) * mm, "end": v(18.14, 5.62) * mm});
            skArc(sketch, "E16.32.22.0", {"start": v(18.35, 4.9) * mm, "mid": v(18.38, 4.96) * mm, "end": v(18.38, 5.03) * mm});
            skArc(sketch, "E16.36.22.0", {"start": v(17.3, 3.95) * mm, "mid": v(17.33, 3.96) * mm, "end": v(17.36, 3.97) * mm});
            skArc(sketch, "E16.40.22.0", {"start": v(15.53, 5.6) * mm, "mid": v(15.61, 5.5) * mm, "end": v(15.73, 5.5) * mm});
            skArc(sketch, "E16.44.22.0", {"start": v(16.24, 3.7) * mm, "mid": v(16.15, 3.64) * mm, "end": v(16.13, 3.53) * mm});
            skArc(sketch, "E16.1.23.0", {"start": v(16.04, 7.74) * mm, "mid": v(16.46, 8.27) * mm, "end": v(16.8, 8.86) * mm});
            skPoint(sketch, "E16.4.23.0", {"position": v(16.51, 9.5) * mm});
            skPoint(sketch, "E16.5.23.0", {"position": v(15.05, 9.46) * mm});
            skLineSegment(sketch, "E16.6.23.0", {"start": v(16, 7.7) * mm, "end": v(15.01, 7.23) * mm});
            skLineSegment(sketch, "E16.9.23.0", {"start": v(15.03, 9.44) * mm, "end": v(14.1, 8.86) * mm});
            skArc(sketch, "E16.12.23.0", {"start": v(15.08, 9.47) * mm, "mid": v(15.76, 9.54) * mm, "end": v(16.44, 9.51) * mm});
            skPoint(sketch, "E16.16.23.0", {"position": v(16.02, 7.71) * mm});
            skPoint(sketch, "E16.17.23.0", {"position": v(16.83, 8.92) * mm});
            skLineSegment(sketch, "E16.18.23.0", {"start": v(16.8, 8.99) * mm, "end": v(16.69, 9.22) * mm});
            skLineSegment(sketch, "E16.21.23.0", {"start": v(16.55, 9.44) * mm, "end": v(16.69, 9.22) * mm});
            skArc(sketch, "E16.24.23.0", {"start": v(15.08, 9.47) * mm, "mid": v(15.06, 9.46) * mm, "end": v(15.03, 9.44) * mm});
            skArc(sketch, "E16.28.23.0", {"start": v(16.55, 9.44) * mm, "mid": v(16.5, 9.49) * mm, "end": v(16.44, 9.51) * mm});
            skArc(sketch, "E16.32.23.0", {"start": v(16.8, 8.86) * mm, "mid": v(16.81, 8.92) * mm, "end": v(16.8, 8.99) * mm});
            skArc(sketch, "E16.36.23.0", {"start": v(16, 7.7) * mm, "mid": v(16.02, 7.72) * mm, "end": v(16.04, 7.74) * mm});
            skArc(sketch, "E16.40.23.0", {"start": v(13.9, 8.91) * mm, "mid": v(14, 8.84) * mm, "end": v(14.1, 8.86) * mm});
            skArc(sketch, "E16.44.23.0", {"start": v(15.01, 7.23) * mm, "mid": v(14.93, 7.14) * mm, "end": v(14.94, 7.03) * mm});
            skArc(sketch, "E16.1.24.0", {"start": v(13.92, 11.11) * mm, "mid": v(14.2, 11.72) * mm, "end": v(14.4, 12.37) * mm});
            skPoint(sketch, "E16.4.24.0", {"position": v(13.98, 12.94) * mm});
            skPoint(sketch, "E16.5.24.0", {"position": v(12.57, 12.57) * mm});
            skLineSegment(sketch, "E16.6.24.0", {"start": v(13.88, 11.07) * mm, "end": v(13.03, 10.39) * mm});
            skLineSegment(sketch, "E16.9.24.0", {"start": v(12.55, 12.55) * mm, "end": v(11.78, 11.78) * mm});
            skArc(sketch, "E16.12.24.0", {"start": v(12.6, 12.58) * mm, "mid": v(13.24, 12.8) * mm, "end": v(13.9, 12.93) * mm});
            skPoint(sketch, "E16.16.24.0", {"position": v(13.9, 11.09) * mm});
            skPoint(sketch, "E16.17.24.0", {"position": v(14.42, 12.45) * mm});
            skLineSegment(sketch, "E16.18.24.0", {"start": v(14.38, 12.5) * mm, "end": v(14.22, 12.7) * mm});
            skLineSegment(sketch, "E16.21.24.0", {"start": v(14.03, 12.89) * mm, "end": v(14.22, 12.7) * mm});
            skArc(sketch, "E16.24.24.0", {"start": v(12.6, 12.58) * mm, "mid": v(12.57, 12.57) * mm, "end": v(12.55, 12.55) * mm});
            skArc(sketch, "E16.28.24.0", {"start": v(14.03, 12.89) * mm, "mid": v(13.98, 12.92) * mm, "end": v(13.9, 12.93) * mm});
            skArc(sketch, "E16.32.24.0", {"start": v(14.4, 12.37) * mm, "mid": v(14.4, 12.44) * mm, "end": v(14.38, 12.5) * mm});
            skArc(sketch, "E16.36.24.0", {"start": v(13.88, 11.07) * mm, "mid": v(13.9, 11.09) * mm, "end": v(13.92, 11.11) * mm});
            skArc(sketch, "E16.40.24.0", {"start": v(11.57, 11.78) * mm, "mid": v(11.67, 11.74) * mm, "end": v(11.78, 11.78) * mm});
            skArc(sketch, "E16.44.24.0", {"start": v(13.03, 10.39) * mm, "mid": v(12.97, 10.29) * mm, "end": v(13, 10.18) * mm});
            skArc(sketch, "E16.1.25.0", {"start": v(11.1, 13.93) * mm, "mid": v(11.24, 14.6) * mm, "end": v(11.3, 15.27) * mm});
            skPoint(sketch, "E16.4.25.0", {"position": v(10.75, 15.72) * mm});
            skPoint(sketch, "E16.5.25.0", {"position": v(9.46, 15.05) * mm});
            skLineSegment(sketch, "E16.6.25.0", {"start": v(11.07, 13.88) * mm, "end": v(10.39, 13.03) * mm});
            skLineSegment(sketch, "E16.9.25.0", {"start": v(9.44, 15.03) * mm, "end": v(8.86, 14.1) * mm});
            skArc(sketch, "E16.12.25.0", {"start": v(9.48, 15.07) * mm, "mid": v(10.06, 15.43) * mm, "end": v(10.68, 15.7) * mm});
            skPoint(sketch, "E16.16.25.0", {"position": v(11.09, 13.9) * mm});
            skPoint(sketch, "E16.17.25.0", {"position": v(11.3, 15.34) * mm});
            skLineSegment(sketch, "E16.18.25.0", {"start": v(11.23, 15.39) * mm, "end": v(11.03, 15.55) * mm});
            skLineSegment(sketch, "E16.21.25.0", {"start": v(10.81, 15.69) * mm, "end": v(11.03, 15.55) * mm});
            skArc(sketch, "E16.24.25.0", {"start": v(9.48, 15.07) * mm, "mid": v(9.46, 15.05) * mm, "end": v(9.44, 15.03) * mm});
            skArc(sketch, "E16.28.25.0", {"start": v(10.81, 15.69) * mm, "mid": v(10.75, 15.7) * mm, "end": v(10.68, 15.7) * mm});
            skArc(sketch, "E16.32.25.0", {"start": v(11.3, 15.27) * mm, "mid": v(11.28, 15.34) * mm, "end": v(11.23, 15.39) * mm});
            skArc(sketch, "E16.36.25.0", {"start": v(11.07, 13.88) * mm, "mid": v(11.08, 13.9) * mm, "end": v(11.1, 13.93) * mm});
            skArc(sketch, "E16.40.25.0", {"start": v(8.66, 14.06) * mm, "mid": v(8.77, 14.04) * mm, "end": v(8.86, 14.1) * mm});
            skArc(sketch, "E16.44.25.0", {"start": v(10.39, 13.03) * mm, "mid": v(10.36, 12.92) * mm, "end": v(10.41, 12.81) * mm});
            skArc(sketch, "E16.1.26.0", {"start": v(7.72, 16.05) * mm, "mid": v(7.72, 16.73) * mm, "end": v(7.61, 17.4) * mm});
            skPoint(sketch, "E16.4.26.0", {"position": v(6.98, 17.72) * mm});
            skPoint(sketch, "E16.5.26.0", {"position": v(5.87, 16.78) * mm});
            skLineSegment(sketch, "E16.6.26.0", {"start": v(7.7, 16) * mm, "end": v(7.23, 15.01) * mm});
            skLineSegment(sketch, "E16.9.26.0", {"start": v(5.86, 16.76) * mm, "end": v(5.5, 15.73) * mm});
            skArc(sketch, "E16.12.26.0", {"start": v(5.9, 16.8) * mm, "mid": v(6.37, 17.28) * mm, "end": v(6.92, 17.69) * mm});
            skPoint(sketch, "E16.16.26.0", {"position": v(7.71, 16.02) * mm});
            skPoint(sketch, "E16.17.26.0", {"position": v(7.6, 17.47) * mm});
            skLineSegment(sketch, "E16.18.26.0", {"start": v(7.53, 17.5) * mm, "end": v(7.3, 17.61) * mm});
            skLineSegment(sketch, "E16.21.26.0", {"start": v(7.05, 17.7) * mm, "end": v(7.3, 17.61) * mm});
            skArc(sketch, "E16.24.26.0", {"start": v(5.9, 16.8) * mm, "mid": v(5.87, 16.78) * mm, "end": v(5.86, 16.76) * mm});
            skArc(sketch, "E16.28.26.0", {"start": v(7.05, 17.7) * mm, "mid": v(6.99, 17.7) * mm, "end": v(6.92, 17.69) * mm});
            skArc(sketch, "E16.32.26.0", {"start": v(7.61, 17.4) * mm, "mid": v(7.58, 17.46) * mm, "end": v(7.53, 17.5) * mm});
            skArc(sketch, "E16.36.26.0", {"start": v(7.7, 16) * mm, "mid": v(7.71, 16.02) * mm, "end": v(7.72, 16.05) * mm});
            skArc(sketch, "E16.40.26.0", {"start": v(5.31, 15.63) * mm, "mid": v(5.43, 15.64) * mm, "end": v(5.5, 15.73) * mm});
            skArc(sketch, "E16.44.26.0", {"start": v(7.23, 15.01) * mm, "mid": v(7.22, 14.9) * mm, "end": v(7.3, 14.8) * mm});
            skArc(sketch, "E16.1.27.0", {"start": v(3.95, 17.36) * mm, "mid": v(3.8, 18.03) * mm, "end": v(3.55, 18.66) * mm});
            skPoint(sketch, "E16.4.27.0", {"position": v(2.87, 18.83) * mm});
            skPoint(sketch, "E16.5.27.0", {"position": v(2, 17.67) * mm});
            skLineSegment(sketch, "E16.6.27.0", {"start": v(3.95, 17.3) * mm, "end": v(3.7, 16.24) * mm});
            skLineSegment(sketch, "E16.9.27.0", {"start": v(1.99, 17.64) * mm, "end": v(1.87, 16.56) * mm});
            skArc(sketch, "E16.12.27.0", {"start": v(2, 17.7) * mm, "mid": v(2.37, 18.27) * mm, "end": v(2.81, 18.78) * mm});
            skPoint(sketch, "E16.16.27.0", {"position": v(3.96, 17.33) * mm});
            skPoint(sketch, "E16.17.27.0", {"position": v(3.52, 18.72) * mm});
            skLineSegment(sketch, "E16.18.27.0", {"start": v(3.45, 18.74) * mm, "end": v(3.2, 18.8) * mm});
            skLineSegment(sketch, "E16.21.27.0", {"start": v(2.94, 18.83) * mm, "end": v(3.2, 18.8) * mm});
            skArc(sketch, "E16.24.27.0", {"start": v(2, 17.7) * mm, "mid": v(2, 17.67) * mm, "end": v(1.99, 17.64) * mm});
            skArc(sketch, "E16.28.27.0", {"start": v(2.94, 18.83) * mm, "mid": v(2.87, 18.82) * mm, "end": v(2.81, 18.78) * mm});
            skArc(sketch, "E16.32.27.0", {"start": v(3.55, 18.66) * mm, "mid": v(3.5, 18.7) * mm, "end": v(3.45, 18.74) * mm});
            skArc(sketch, "E16.36.27.0", {"start": v(3.95, 17.3) * mm, "mid": v(3.95, 17.33) * mm, "end": v(3.95, 17.36) * mm});
            skArc(sketch, "E16.40.27.0", {"start": v(1.7, 16.42) * mm, "mid": v(1.8, 16.46) * mm, "end": v(1.87, 16.56) * mm});
            skArc(sketch, "E16.44.27.0", {"start": v(3.7, 16.24) * mm, "mid": v(3.73, 16.13) * mm, "end": v(3.82, 16.06) * mm});
            skArc(sketch, "E17.trimOffspring", {"start": v(-11.78, 11.57) * mm, "mid": v(-12.31, 11) * mm, "end": v(-12.81, 10.41) * mm});
            skArc(sketch, "E18.trimOffspring", {"start": v(-8.91, 13.9) * mm, "mid": v(-9.55, 13.46) * mm, "end": v(-10.18, 13) * mm});
            skArc(sketch, "E19.trimOffspring", {"start": v(-5.6, 15.53) * mm, "mid": v(-6.32, 15.25) * mm, "end": v(-7.03, 14.94) * mm});
            skArc(sketch, "E20.trimOffspring", {"start": v(-14.06, 8.66) * mm, "mid": v(-14.45, 7.99) * mm, "end": v(-14.8, 7.3) * mm});
            skArc(sketch, "E21.trimOffspring", {"start": v(1.7, 16.42) * mm, "mid": v(0.93, 16.48) * mm, "end": v(0.15, 16.5) * mm});
            skArc(sketch, "E22.trimOffspring", {"start": v(5.31, 15.63) * mm, "mid": v(4.57, 15.86) * mm, "end": v(3.82, 16.06) * mm});
            skArc(sketch, "E23.trimOffspring", {"start": v(8.66, 14.06) * mm, "mid": v(7.99, 14.45) * mm, "end": v(7.3, 14.8) * mm});
            skArc(sketch, "E24.trimOffspring", {"start": v(11.57, 11.78) * mm, "mid": v(11, 12.31) * mm, "end": v(10.41, 12.81) * mm});
            skArc(sketch, "E25.trimOffspring", {"start": v(13.9, 8.91) * mm, "mid": v(13.46, 9.55) * mm, "end": v(13, 10.18) * mm});
            skArc(sketch, "E26.trimOffspring", {"start": v(15.53, 5.6) * mm, "mid": v(15.25, 6.32) * mm, "end": v(14.94, 7.03) * mm});
            skArc(sketch, "E27.trimOffspring", {"start": v(16.39, 2) * mm, "mid": v(16.28, 2.77) * mm, "end": v(16.13, 3.53) * mm});
            skArc(sketch, "E28.trimOffspring", {"start": v(16.42, -1.7) * mm, "mid": v(16.48, -0.93) * mm, "end": v(16.5, -0.15) * mm});
            skArc(sketch, "E29.trimOffspring", {"start": v(15.63, -5.31) * mm, "mid": v(15.86, -4.57) * mm, "end": v(16.06, -3.82) * mm});
            skArc(sketch, "E30.trimOffspring", {"start": v(14.06, -8.66) * mm, "mid": v(14.45, -7.99) * mm, "end": v(14.8, -7.3) * mm});
            skArc(sketch, "E31.trimOffspring", {"start": v(11.78, -11.57) * mm, "mid": v(12.31, -11) * mm, "end": v(12.81, -10.41) * mm});
            skArc(sketch, "E32.trimOffspring", {"start": v(8.91, -13.9) * mm, "mid": v(9.55, -13.46) * mm, "end": v(10.18, -13) * mm});
            skArc(sketch, "E33.trimOffspring", {"start": v(5.6, -15.53) * mm, "mid": v(6.32, -15.25) * mm, "end": v(7.03, -14.94) * mm});
            skArc(sketch, "E34.trimOffspring", {"start": v(2, -16.39) * mm, "mid": v(2.77, -16.28) * mm, "end": v(3.53, -16.13) * mm});
            skArc(sketch, "E35.trimOffspring", {"start": v(-1.7, -16.42) * mm, "mid": v(-0.93, -16.48) * mm, "end": v(-0.15, -16.5) * mm});
            skArc(sketch, "E36.trimOffspring", {"start": v(-5.31, -15.63) * mm, "mid": v(-4.57, -15.86) * mm, "end": v(-3.82, -16.06) * mm});
            skArc(sketch, "E37.trimOffspring", {"start": v(-8.66, -14.06) * mm, "mid": v(-7.99, -14.45) * mm, "end": v(-7.3, -14.8) * mm});
            skArc(sketch, "E38.trimOffspring", {"start": v(-11.57, -11.78) * mm, "mid": v(-11, -12.31) * mm, "end": v(-10.41, -12.81) * mm});
            skArc(sketch, "E39.trimOffspring", {"start": v(-13.9, -8.91) * mm, "mid": v(-13.46, -9.55) * mm, "end": v(-13, -10.18) * mm});
            skArc(sketch, "E40.trimOffspring", {"start": v(-15.53, -5.6) * mm, "mid": v(-15.25, -6.32) * mm, "end": v(-14.94, -7.03) * mm});
            skArc(sketch, "E41.trimOffspring", {"start": v(-16.39, -2) * mm, "mid": v(-16.28, -2.77) * mm, "end": v(-16.13, -3.53) * mm});
            skArc(sketch, "E42.trimOffspring", {"start": v(-16.42, 1.7) * mm, "mid": v(-16.48, 0.93) * mm, "end": v(-16.5, 0.15) * mm});
            skArc(sketch, "E43.trimOffspring", {"start": v(-15.63, 5.31) * mm, "mid": v(-15.86, 4.57) * mm, "end": v(-16.06, 3.82) * mm});
            skSolve(sketch);
        }
        {
            var Q0;
            Q0 = qSketchRegion(id + "F0", true);
            extrude(context, id + "F1", {"entities" : qUnion([Q0]), "depth" : 6.35 * mm});
        }
        {
            var Q0;
            Q0=makeQuery(id+"F1.opExtrude","CAP_FACE",FACE,{"disambiguationData":[OSD([sQuery(id+"F0.wireOp",EDGE,"E0"),sQuery(id+"F0.wireOp",EDGE,"E1.trimOffspring"),sQuery(id+"F0.wireOp",EDGE,"E2"),sQuery(id+"F0.wireOp",EDGE,"E3"),sQuery(id+"F0.wireOp",EDGE,"E4.MirrorCS"),sQuery(id+"F0.wireOp",EDGE,"E5.MirrorCS"),sQuery(id+"F0.wireOp",EDGE,"E6.MirrorCS"),sQuery(id+"F0.wireOp",EDGE,"E9.filletArc"),sQuery(id+"F0.wireOp",EDGE,"E10.filletArc"),sQuery(id+"F0.wireOp",EDGE,"E11.filletArc"),sQuery(id+"F0.wireOp",EDGE,"E12.filletArc"),sQuery(id+"F0.wireOp",EDGE,"E13.filletArc"),sQuery(id+"F0.wireOp",EDGE,"E14.filletArc"),sQuery(id+"F0.wireOp",EDGE,"E15.1.0"),sQuery(id+"F0.wireOp",EDGE,"E15.1.3"),sQuery(id+"F0.wireOp",EDGE,"E15.1.4"),sQuery(id+"F0.wireOp",EDGE,"E15.1.5"),sQuery(id+"F0.wireOp",EDGE,"E15.1.8"),sQuery(id+"F0.wireOp",EDGE,"E15.1.9"),sQuery(id+"F0.wireOp",EDGE,"E15.1.10"),sQuery(id+"F0.wireOp",EDGE,"E15.1.11"),sQuery(id+"F0.wireOp",EDGE,"E15.1.12"),sQuery(id+"F0.wireOp",EDGE,"E15.1.13"),sQuery(id+"F0.wireOp",EDGE,"E15.1.14"),sQuery(id+"F0.wireOp",EDGE,"E15.1.15"),sQuery(id+"F0.wireOp",EDGE,"E15.2.0"),sQuery(id+"F0.wireOp",EDGE,"E15.2.3"),sQuery(id+"F0.wireOp",EDGE,"E15.2.4"),sQuery(id+"F0.wireOp",EDGE,"E15.2.5"),sQuery(id+"F0.wireOp",EDGE,"E15.2.8"),sQuery(id+"F0.wireOp",EDGE,"E15.2.9"),sQuery(id+"F0.wireOp",EDGE,"E15.2.10"),sQuery(id+"F0.wireOp",EDGE,"E15.2.11"),sQuery(id+"F0.wireOp",EDGE,"E15.2.12"),sQuery(id+"F0.wireOp",EDGE,"E15.2.13"),sQuery(id+"F0.wireOp",EDGE,"E15.2.14"),sQuery(id+"F0.wireOp",EDGE,"E15.2.15"),sQuery(id+"F0.wireOp",EDGE,"E16.1.3.0"),sQuery(id+"F0.wireOp",EDGE,"E16.6.3.0"),sQuery(id+"F0.wireOp",EDGE,"E16.9.3.0"),sQuery(id+"F0.wireOp",EDGE,"E16.12.3.0"),sQuery(id+"F0.wireOp",EDGE,"E16.18.3.0"),sQuery(id+"F0.wireOp",EDGE,"E16.21.3.0"),sQuery(id+"F0.wireOp",EDGE,"E16.24.3.0"),sQuery(id+"F0.wireOp",EDGE,"E16.28.3.0"),sQuery(id+"F0.wireOp",EDGE,"E16.32.3.0"),sQuery(id+"F0.wireOp",EDGE,"E16.36.3.0"),sQuery(id+"F0.wireOp",EDGE,"E16.40.3.0"),sQuery(id+"F0.wireOp",EDGE,"E16.44.3.0"),sQuery(id+"F0.wireOp",EDGE,"E16.1.4.0"),sQuery(id+"F0.wireOp",EDGE,"E16.6.4.0"),sQuery(id+"F0.wireOp",EDGE,"E16.9.4.0"),sQuery(id+"F0.wireOp",EDGE,"E16.12.4.0"),sQuery(id+"F0.wireOp",EDGE,"E16.18.4.0"),sQuery(id+"F0.wireOp",EDGE,"E16.21.4.0"),sQuery(id+"F0.wireOp",EDGE,"E16.24.4.0"),sQuery(id+"F0.wireOp",EDGE,"E16.28.4.0"),sQuery(id+"F0.wireOp",EDGE,"E16.32.4.0"),sQuery(id+"F0.wireOp",EDGE,"E16.36.4.0"),sQuery(id+"F0.wireOp",EDGE,"E16.40.4.0"),sQuery(id+"F0.wireOp",EDGE,"E16.44.4.0"),sQuery(id+"F0.wireOp",EDGE,"E16.1.5.0"),sQuery(id+"F0.wireOp",EDGE,"E16.6.5.0"),sQuery(id+"F0.wireOp",EDGE,"E16.9.5.0"),sQuery(id+"F0.wireOp",EDGE,"E16.12.5.0"),sQuery(id+"F0.wireOp",EDGE,"E16.18.5.0"),sQuery(id+"F0.wireOp",EDGE,"E16.21.5.0"),sQuery(id+"F0.wireOp",EDGE,"E16.24.5.0"),sQuery(id+"F0.wireOp",EDGE,"E16.28.5.0"),sQuery(id+"F0.wireOp",EDGE,"E16.32.5.0"),sQuery(id+"F0.wireOp",EDGE,"E16.36.5.0"),sQuery(id+"F0.wireOp",EDGE,"E16.40.5.0"),sQuery(id+"F0.wireOp",EDGE,"E16.44.5.0"),sQuery(id+"F0.wireOp",EDGE,"E16.1.6.0"),sQuery(id+"F0.wireOp",EDGE,"E16.6.6.0"),sQuery(id+"F0.wireOp",EDGE,"E16.9.6.0"),sQuery(id+"F0.wireOp",EDGE,"E16.12.6.0"),sQuery(id+"F0.wireOp",EDGE,"E16.18.6.0"),sQuery(id+"F0.wireOp",EDGE,"E16.21.6.0"),sQuery(id+"F0.wireOp",EDGE,"E16.24.6.0"),sQuery(id+"F0.wireOp",EDGE,"E16.28.6.0"),sQuery(id+"F0.wireOp",EDGE,"E16.32.6.0"),sQuery(id+"F0.wireOp",EDGE,"E16.36.6.0"),sQuery(id+"F0.wireOp",EDGE,"E16.40.6.0"),sQuery(id+"F0.wireOp",EDGE,"E16.44.6.0"),sQuery(id+"F0.wireOp",EDGE,"E16.1.7.0"),sQuery(id+"F0.wireOp",EDGE,"E16.6.7.0"),sQuery(id+"F0.wireOp",EDGE,"E16.9.7.0"),sQuery(id+"F0.wireOp",EDGE,"E16.12.7.0"),sQuery(id+"F0.wireOp",EDGE,"E16.18.7.0"),sQuery(id+"F0.wireOp",EDGE,"E16.21.7.0"),sQuery(id+"F0.wireOp",EDGE,"E16.24.7.0"),sQuery(id+"F0.wireOp",EDGE,"E16.28.7.0"),sQuery(id+"F0.wireOp",EDGE,"E16.32.7.0"),sQuery(id+"F0.wireOp",EDGE,"E16.36.7.0"),sQuery(id+"F0.wireOp",EDGE,"E16.40.7.0"),sQuery(id+"F0.wireOp",EDGE,"E16.44.7.0"),sQuery(id+"F0.wireOp",EDGE,"E16.1.8.0"),sQuery(id+"F0.wireOp",EDGE,"E16.6.8.0"),sQuery(id+"F0.wireOp",EDGE,"E16.9.8.0"),sQuery(id+"F0.wireOp",EDGE,"E16.12.8.0"),sQuery(id+"F0.wireOp",EDGE,"E16.18.8.0"),sQuery(id+"F0.wireOp",EDGE,"E16.21.8.0"),sQuery(id+"F0.wireOp",EDGE,"E16.24.8.0"),sQuery(id+"F0.wireOp",EDGE,"E16.28.8.0"),sQuery(id+"F0.wireOp",EDGE,"E16.32.8.0"),sQuery(id+"F0.wireOp",EDGE,"E16.36.8.0"),sQuery(id+"F0.wireOp",EDGE,"E16.40.8.0"),sQuery(id+"F0.wireOp",EDGE,"E16.44.8.0"),sQuery(id+"F0.wireOp",EDGE,"E16.1.9.0"),sQuery(id+"F0.wireOp",EDGE,"E16.6.9.0"),sQuery(id+"F0.wireOp",EDGE,"E16.9.9.0"),sQuery(id+"F0.wireOp",EDGE,"E16.12.9.0"),sQuery(id+"F0.wireOp",EDGE,"E16.18.9.0"),sQuery(id+"F0.wireOp",EDGE,"E16.21.9.0"),sQuery(id+"F0.wireOp",EDGE,"E16.24.9.0"),sQuery(id+"F0.wireOp",EDGE,"E16.28.9.0"),sQuery(id+"F0.wireOp",EDGE,"E16.32.9.0"),sQuery(id+"F0.wireOp",EDGE,"E16.36.9.0"),sQuery(id+"F0.wireOp",EDGE,"E16.40.9.0"),sQuery(id+"F0.wireOp",EDGE,"E16.44.9.0"),sQuery(id+"F0.wireOp",EDGE,"E16.1.10.0"),sQuery(id+"F0.wireOp",EDGE,"E16.6.10.0"),sQuery(id+"F0.wireOp",EDGE,"E16.9.10.0"),sQuery(id+"F0.wireOp",EDGE,"E16.12.10.0"),sQuery(id+"F0.wireOp",EDGE,"E16.18.10.0"),sQuery(id+"F0.wireOp",EDGE,"E16.21.10.0"),sQuery(id+"F0.wireOp",EDGE,"E16.24.10.0"),sQuery(id+"F0.wireOp",EDGE,"E16.28.10.0"),sQuery(id+"F0.wireOp",EDGE,"E16.32.10.0"),sQuery(id+"F0.wireOp",EDGE,"E16.36.10.0"),sQuery(id+"F0.wireOp",EDGE,"E16.40.10.0"),sQuery(id+"F0.wireOp",EDGE,"E16.44.10.0"),sQuery(id+"F0.wireOp",EDGE,"E16.1.11.0"),sQuery(id+"F0.wireOp",EDGE,"E16.6.11.0"),sQuery(id+"F0.wireOp",EDGE,"E16.9.11.0"),sQuery(id+"F0.wireOp",EDGE,"E16.12.11.0"),sQuery(id+"F0.wireOp",EDGE,"E16.18.11.0"),sQuery(id+"F0.wireOp",EDGE,"E16.21.11.0"),sQuery(id+"F0.wireOp",EDGE,"E16.24.11.0"),sQuery(id+"F0.wireOp",EDGE,"E16.28.11.0"),sQuery(id+"F0.wireOp",EDGE,"E16.32.11.0"),sQuery(id+"F0.wireOp",EDGE,"E16.36.11.0"),sQuery(id+"F0.wireOp",EDGE,"E16.40.11.0"),sQuery(id+"F0.wireOp",EDGE,"E16.44.11.0"),sQuery(id+"F0.wireOp",EDGE,"E16.1.12.0"),sQuery(id+"F0.wireOp",EDGE,"E16.6.12.0"),sQuery(id+"F0.wireOp",EDGE,"E16.9.12.0"),sQuery(id+"F0.wireOp",EDGE,"E16.12.12.0"),sQuery(id+"F0.wireOp",EDGE,"E16.18.12.0"),sQuery(id+"F0.wireOp",EDGE,"E16.21.12.0"),sQuery(id+"F0.wireOp",EDGE,"E16.24.12.0"),sQuery(id+"F0.wireOp",EDGE,"E16.28.12.0"),sQuery(id+"F0.wireOp",EDGE,"E16.32.12.0"),sQuery(id+"F0.wireOp",EDGE,"E16.36.12.0"),sQuery(id+"F0.wireOp",EDGE,"E16.40.12.0"),sQuery(id+"F0.wireOp",EDGE,"E16.44.12.0"),sQuery(id+"F0.wireOp",EDGE,"E16.1.13.0"),sQuery(id+"F0.wireOp",EDGE,"E16.6.13.0"),sQuery(id+"F0.wireOp",EDGE,"E16.9.13.0"),sQuery(id+"F0.wireOp",EDGE,"E16.12.13.0"),sQuery(id+"F0.wireOp",EDGE,"E16.18.13.0"),sQuery(id+"F0.wireOp",EDGE,"E16.21.13.0"),sQuery(id+"F0.wireOp",EDGE,"E16.24.13.0"),sQuery(id+"F0.wireOp",EDGE,"E16.28.13.0"),sQuery(id+"F0.wireOp",EDGE,"E16.32.13.0"),sQuery(id+"F0.wireOp",EDGE,"E16.36.13.0"),sQuery(id+"F0.wireOp",EDGE,"E16.40.13.0"),sQuery(id+"F0.wireOp",EDGE,"E16.44.13.0"),sQuery(id+"F0.wireOp",EDGE,"E16.1.14.0"),sQuery(id+"F0.wireOp",EDGE,"E16.6.14.0"),sQuery(id+"F0.wireOp",EDGE,"E16.9.14.0"),sQuery(id+"F0.wireOp",EDGE,"E16.12.14.0"),sQuery(id+"F0.wireOp",EDGE,"E16.18.14.0"),sQuery(id+"F0.wireOp",EDGE,"E16.21.14.0"),sQuery(id+"F0.wireOp",EDGE,"E16.24.14.0"),sQuery(id+"F0.wireOp",EDGE,"E16.28.14.0"),sQuery(id+"F0.wireOp",EDGE,"E16.32.14.0"),sQuery(id+"F0.wireOp",EDGE,"E16.36.14.0"),sQuery(id+"F0.wireOp",EDGE,"E16.40.14.0"),sQuery(id+"F0.wireOp",EDGE,"E16.44.14.0"),sQuery(id+"F0.wireOp",EDGE,"E16.1.15.0"),sQuery(id+"F0.wireOp",EDGE,"E16.6.15.0"),sQuery(id+"F0.wireOp",EDGE,"E16.9.15.0"),sQuery(id+"F0.wireOp",EDGE,"E16.12.15.0"),sQuery(id+"F0.wireOp",EDGE,"E16.18.15.0"),sQuery(id+"F0.wireOp",EDGE,"E16.21.15.0"),sQuery(id+"F0.wireOp",EDGE,"E16.24.15.0"),sQuery(id+"F0.wireOp",EDGE,"E16.28.15.0"),sQuery(id+"F0.wireOp",EDGE,"E16.32.15.0"),sQuery(id+"F0.wireOp",EDGE,"E16.36.15.0"),sQuery(id+"F0.wireOp",EDGE,"E16.40.15.0"),sQuery(id+"F0.wireOp",EDGE,"E16.44.15.0"),sQuery(id+"F0.wireOp",EDGE,"E16.1.16.0"),sQuery(id+"F0.wireOp",EDGE,"E16.6.16.0"),sQuery(id+"F0.wireOp",EDGE,"E16.9.16.0"),sQuery(id+"F0.wireOp",EDGE,"E16.12.16.0"),sQuery(id+"F0.wireOp",EDGE,"E16.18.16.0"),sQuery(id+"F0.wireOp",EDGE,"E16.21.16.0"),sQuery(id+"F0.wireOp",EDGE,"E16.24.16.0"),sQuery(id+"F0.wireOp",EDGE,"E16.28.16.0"),sQuery(id+"F0.wireOp",EDGE,"E16.32.16.0"),sQuery(id+"F0.wireOp",EDGE,"E16.36.16.0"),sQuery(id+"F0.wireOp",EDGE,"E16.40.16.0"),sQuery(id+"F0.wireOp",EDGE,"E16.44.16.0"),sQuery(id+"F0.wireOp",EDGE,"E16.1.17.0"),sQuery(id+"F0.wireOp",EDGE,"E16.6.17.0"),sQuery(id+"F0.wireOp",EDGE,"E16.9.17.0"),sQuery(id+"F0.wireOp",EDGE,"E16.12.17.0"),sQuery(id+"F0.wireOp",EDGE,"E16.18.17.0"),sQuery(id+"F0.wireOp",EDGE,"E16.21.17.0"),sQuery(id+"F0.wireOp",EDGE,"E16.24.17.0"),sQuery(id+"F0.wireOp",EDGE,"E16.28.17.0"),sQuery(id+"F0.wireOp",EDGE,"E16.32.17.0"),sQuery(id+"F0.wireOp",EDGE,"E16.36.17.0"),sQuery(id+"F0.wireOp",EDGE,"E16.40.17.0"),sQuery(id+"F0.wireOp",EDGE,"E16.44.17.0"),sQuery(id+"F0.wireOp",EDGE,"E16.1.18.0"),sQuery(id+"F0.wireOp",EDGE,"E16.6.18.0"),sQuery(id+"F0.wireOp",EDGE,"E16.9.18.0"),sQuery(id+"F0.wireOp",EDGE,"E16.12.18.0"),sQuery(id+"F0.wireOp",EDGE,"E16.18.18.0"),sQuery(id+"F0.wireOp",EDGE,"E16.21.18.0"),sQuery(id+"F0.wireOp",EDGE,"E16.24.18.0"),sQuery(id+"F0.wireOp",EDGE,"E16.28.18.0"),sQuery(id+"F0.wireOp",EDGE,"E16.32.18.0"),sQuery(id+"F0.wireOp",EDGE,"E16.36.18.0"),sQuery(id+"F0.wireOp",EDGE,"E16.40.18.0"),sQuery(id+"F0.wireOp",EDGE,"E16.44.18.0"),sQuery(id+"F0.wireOp",EDGE,"E16.1.19.0"),sQuery(id+"F0.wireOp",EDGE,"E16.6.19.0"),sQuery(id+"F0.wireOp",EDGE,"E16.9.19.0"),sQuery(id+"F0.wireOp",EDGE,"E16.12.19.0"),sQuery(id+"F0.wireOp",EDGE,"E16.18.19.0"),sQuery(id+"F0.wireOp",EDGE,"E16.21.19.0"),sQuery(id+"F0.wireOp",EDGE,"E16.24.19.0"),sQuery(id+"F0.wireOp",EDGE,"E16.28.19.0"),sQuery(id+"F0.wireOp",EDGE,"E16.32.19.0"),sQuery(id+"F0.wireOp",EDGE,"E16.36.19.0"),sQuery(id+"F0.wireOp",EDGE,"E16.40.19.0"),sQuery(id+"F0.wireOp",EDGE,"E16.44.19.0"),sQuery(id+"F0.wireOp",EDGE,"E16.1.20.0"),sQuery(id+"F0.wireOp",EDGE,"E16.6.20.0"),sQuery(id+"F0.wireOp",EDGE,"E16.9.20.0"),sQuery(id+"F0.wireOp",EDGE,"E16.12.20.0"),sQuery(id+"F0.wireOp",EDGE,"E16.18.20.0"),sQuery(id+"F0.wireOp",EDGE,"E16.21.20.0"),sQuery(id+"F0.wireOp",EDGE,"E16.24.20.0"),sQuery(id+"F0.wireOp",EDGE,"E16.28.20.0"),sQuery(id+"F0.wireOp",EDGE,"E16.32.20.0"),sQuery(id+"F0.wireOp",EDGE,"E16.36.20.0"),sQuery(id+"F0.wireOp",EDGE,"E16.40.20.0"),sQuery(id+"F0.wireOp",EDGE,"E16.44.20.0"),sQuery(id+"F0.wireOp",EDGE,"E16.1.21.0"),sQuery(id+"F0.wireOp",EDGE,"E16.6.21.0"),sQuery(id+"F0.wireOp",EDGE,"E16.9.21.0"),sQuery(id+"F0.wireOp",EDGE,"E16.12.21.0"),sQuery(id+"F0.wireOp",EDGE,"E16.18.21.0"),sQuery(id+"F0.wireOp",EDGE,"E16.21.21.0"),sQuery(id+"F0.wireOp",EDGE,"E16.24.21.0"),sQuery(id+"F0.wireOp",EDGE,"E16.28.21.0"),sQuery(id+"F0.wireOp",EDGE,"E16.32.21.0"),sQuery(id+"F0.wireOp",EDGE,"E16.36.21.0"),sQuery(id+"F0.wireOp",EDGE,"E16.40.21.0"),sQuery(id+"F0.wireOp",EDGE,"E16.44.21.0"),sQuery(id+"F0.wireOp",EDGE,"E16.1.22.0"),sQuery(id+"F0.wireOp",EDGE,"E16.6.22.0"),sQuery(id+"F0.wireOp",EDGE,"E16.9.22.0"),sQuery(id+"F0.wireOp",EDGE,"E16.12.22.0"),sQuery(id+"F0.wireOp",EDGE,"E16.18.22.0"),sQuery(id+"F0.wireOp",EDGE,"E16.21.22.0"),sQuery(id+"F0.wireOp",EDGE,"E16.24.22.0"),sQuery(id+"F0.wireOp",EDGE,"E16.28.22.0"),sQuery(id+"F0.wireOp",EDGE,"E16.32.22.0"),sQuery(id+"F0.wireOp",EDGE,"E16.36.22.0"),sQuery(id+"F0.wireOp",EDGE,"E16.40.22.0"),sQuery(id+"F0.wireOp",EDGE,"E16.44.22.0"),sQuery(id+"F0.wireOp",EDGE,"E16.1.23.0"),sQuery(id+"F0.wireOp",EDGE,"E16.6.23.0"),sQuery(id+"F0.wireOp",EDGE,"E16.9.23.0"),sQuery(id+"F0.wireOp",EDGE,"E16.12.23.0"),sQuery(id+"F0.wireOp",EDGE,"E16.18.23.0"),sQuery(id+"F0.wireOp",EDGE,"E16.21.23.0"),sQuery(id+"F0.wireOp",EDGE,"E16.24.23.0"),sQuery(id+"F0.wireOp",EDGE,"E16.28.23.0"),sQuery(id+"F0.wireOp",EDGE,"E16.32.23.0"),sQuery(id+"F0.wireOp",EDGE,"E16.36.23.0"),sQuery(id+"F0.wireOp",EDGE,"E16.40.23.0"),sQuery(id+"F0.wireOp",EDGE,"E16.44.23.0"),sQuery(id+"F0.wireOp",EDGE,"E16.1.24.0"),sQuery(id+"F0.wireOp",EDGE,"E16.6.24.0"),sQuery(id+"F0.wireOp",EDGE,"E16.9.24.0"),sQuery(id+"F0.wireOp",EDGE,"E16.12.24.0"),sQuery(id+"F0.wireOp",EDGE,"E16.18.24.0"),sQuery(id+"F0.wireOp",EDGE,"E16.21.24.0"),sQuery(id+"F0.wireOp",EDGE,"E16.24.24.0"),sQuery(id+"F0.wireOp",EDGE,"E16.28.24.0"),sQuery(id+"F0.wireOp",EDGE,"E16.32.24.0"),sQuery(id+"F0.wireOp",EDGE,"E16.36.24.0"),sQuery(id+"F0.wireOp",EDGE,"E16.40.24.0"),sQuery(id+"F0.wireOp",EDGE,"E16.44.24.0"),sQuery(id+"F0.wireOp",EDGE,"E16.1.25.0"),sQuery(id+"F0.wireOp",EDGE,"E16.6.25.0"),sQuery(id+"F0.wireOp",EDGE,"E16.9.25.0"),sQuery(id+"F0.wireOp",EDGE,"E16.12.25.0"),sQuery(id+"F0.wireOp",EDGE,"E16.18.25.0"),sQuery(id+"F0.wireOp",EDGE,"E16.21.25.0"),sQuery(id+"F0.wireOp",EDGE,"E16.24.25.0"),sQuery(id+"F0.wireOp",EDGE,"E16.28.25.0"),sQuery(id+"F0.wireOp",EDGE,"E16.32.25.0"),sQuery(id+"F0.wireOp",EDGE,"E16.36.25.0"),sQuery(id+"F0.wireOp",EDGE,"E16.40.25.0"),sQuery(id+"F0.wireOp",EDGE,"E16.44.25.0"),sQuery(id+"F0.wireOp",EDGE,"E16.1.26.0"),sQuery(id+"F0.wireOp",EDGE,"E16.6.26.0"),sQuery(id+"F0.wireOp",EDGE,"E16.9.26.0"),sQuery(id+"F0.wireOp",EDGE,"E16.12.26.0"),sQuery(id+"F0.wireOp",EDGE,"E16.18.26.0"),sQuery(id+"F0.wireOp",EDGE,"E16.21.26.0"),sQuery(id+"F0.wireOp",EDGE,"E16.24.26.0"),sQuery(id+"F0.wireOp",EDGE,"E16.28.26.0"),sQuery(id+"F0.wireOp",EDGE,"E16.32.26.0"),sQuery(id+"F0.wireOp",EDGE,"E16.36.26.0"),sQuery(id+"F0.wireOp",EDGE,"E16.40.26.0"),sQuery(id+"F0.wireOp",EDGE,"E16.44.26.0"),sQuery(id+"F0.wireOp",EDGE,"E16.1.27.0"),sQuery(id+"F0.wireOp",EDGE,"E16.6.27.0"),sQuery(id+"F0.wireOp",EDGE,"E16.9.27.0"),sQuery(id+"F0.wireOp",EDGE,"E16.12.27.0"),sQuery(id+"F0.wireOp",EDGE,"E16.18.27.0"),sQuery(id+"F0.wireOp",EDGE,"E16.21.27.0"),sQuery(id+"F0.wireOp",EDGE,"E16.24.27.0"),sQuery(id+"F0.wireOp",EDGE,"E16.28.27.0"),sQuery(id+"F0.wireOp",EDGE,"E16.32.27.0"),sQuery(id+"F0.wireOp",EDGE,"E16.36.27.0"),sQuery(id+"F0.wireOp",EDGE,"E16.40.27.0"),sQuery(id+"F0.wireOp",EDGE,"E16.44.27.0"),sQuery(id+"F0.wireOp",EDGE,"E17.trimOffspring"),sQuery(id+"F0.wireOp",EDGE,"E18.trimOffspring"),sQuery(id+"F0.wireOp",EDGE,"E19.trimOffspring"),sQuery(id+"F0.wireOp",EDGE,"E20.trimOffspring"),sQuery(id+"F0.wireOp",EDGE,"E21.trimOffspring"),sQuery(id+"F0.wireOp",EDGE,"E22.trimOffspring"),sQuery(id+"F0.wireOp",EDGE,"E23.trimOffspring"),sQuery(id+"F0.wireOp",EDGE,"E24.trimOffspring"),sQuery(id+"F0.wireOp",EDGE,"E25.trimOffspring"),sQuery(id+"F0.wireOp",EDGE,"E26.trimOffspring"),sQuery(id+"F0.wireOp",EDGE,"E27.trimOffspring"),sQuery(id+"F0.wireOp",EDGE,"E28.trimOffspring"),sQuery(id+"F0.wireOp",EDGE,"E29.trimOffspring"),sQuery(id+"F0.wireOp",EDGE,"E30.trimOffspring"),sQuery(id+"F0.wireOp",EDGE,"E31.trimOffspring"),sQuery(id+"F0.wireOp",EDGE,"E32.trimOffspring"),sQuery(id+"F0.wireOp",EDGE,"E33.trimOffspring"),sQuery(id+"F0.wireOp",EDGE,"E34.trimOffspring"),sQuery(id+"F0.wireOp",EDGE,"E35.trimOffspring"),sQuery(id+"F0.wireOp",EDGE,"E36.trimOffspring"),sQuery(id+"F0.wireOp",EDGE,"E37.trimOffspring"),sQuery(id+"F0.wireOp",EDGE,"E38.trimOffspring"),sQuery(id+"F0.wireOp",EDGE,"E39.trimOffspring"),sQuery(id+"F0.wireOp",EDGE,"E40.trimOffspring"),sQuery(id+"F0.wireOp",EDGE,"E41.trimOffspring"),sQuery(id+"F0.wireOp",EDGE,"E42.trimOffspring"),sQuery(id+"F0.wireOp",EDGE,"E43.trimOffspring")])],"isStart":false});
            var sketch = newSketch(context, id + "F2", { "sketchPlane" : qUnion([Q0])});
            skCircle(sketch, "E44", {"center": v(0, 0) * mm, "radius": 6.35 * mm});
            skSolve(sketch);
        }
        {
            var Q0;
            Q0 = qSketchRegion(id + "F2", true);
            var Q1;
            Q1=makeQuery(id+"F2.imprint","IMPRINT",FACE,{"disambiguationData":[TD([[makeQuery(id+"F2.imprint","IMPRINT",EDGE,{"derivedFrom":sQuery(id+"F2.wireOp",EDGE,"E44")}),1.0]])]});
            extrude(context, id + "F3", {"entities" : qUnion([Q0, Q1]), "operationType" : NewBodyOperationType.ADD, "depth" : 6.35 * mm});
        }
        {
            var Q0;
            Q0=makeQuery(id+"F3.opExtrude","CAP_FACE",FACE,{"disambiguationData":[OSD([sQuery(id+"F2.wireOp",EDGE,"E44")])],"isStart":false});
            var sketch = newSketch(context, id + "F4", { "sketchPlane" : qUnion([Q0])});
            skPoint(sketch, "E45", {"position": v(0, 0) * mm});
            skSolve(sketch);
        }
        {
            var Q0;
            Q0=sQuery(id+"F4.wireOp",VERTEX,"E45");
            var Q1;
            Q1=makeQuery(id+"F1.opExtrude","SWEPT_BODY",BODY,{"disambiguationData":[OSD([sQuery(id+"F0.wireOp",EDGE,"E0"),sQuery(id+"F0.wireOp",EDGE,"E1.trimOffspring"),sQuery(id+"F0.wireOp",EDGE,"E2"),sQuery(id+"F0.wireOp",EDGE,"E3"),sQuery(id+"F0.wireOp",EDGE,"E4.MirrorCS"),sQuery(id+"F0.wireOp",EDGE,"E5.MirrorCS"),sQuery(id+"F0.wireOp",EDGE,"E6.MirrorCS"),sQuery(id+"F0.wireOp",EDGE,"E9.filletArc"),sQuery(id+"F0.wireOp",EDGE,"E10.filletArc"),sQuery(id+"F0.wireOp",EDGE,"E11.filletArc"),sQuery(id+"F0.wireOp",EDGE,"E12.filletArc"),sQuery(id+"F0.wireOp",EDGE,"E13.filletArc"),sQuery(id+"F0.wireOp",EDGE,"E14.filletArc"),sQuery(id+"F0.wireOp",EDGE,"E15.1.0"),sQuery(id+"F0.wireOp",EDGE,"E15.1.3"),sQuery(id+"F0.wireOp",EDGE,"E15.1.4"),sQuery(id+"F0.wireOp",EDGE,"E15.1.5"),sQuery(id+"F0.wireOp",EDGE,"E15.1.8"),sQuery(id+"F0.wireOp",EDGE,"E15.1.9"),sQuery(id+"F0.wireOp",EDGE,"E15.1.10"),sQuery(id+"F0.wireOp",EDGE,"E15.1.11"),sQuery(id+"F0.wireOp",EDGE,"E15.1.12"),sQuery(id+"F0.wireOp",EDGE,"E15.1.13"),sQuery(id+"F0.wireOp",EDGE,"E15.1.14"),sQuery(id+"F0.wireOp",EDGE,"E15.1.15"),sQuery(id+"F0.wireOp",EDGE,"E15.2.0"),sQuery(id+"F0.wireOp",EDGE,"E15.2.3"),sQuery(id+"F0.wireOp",EDGE,"E15.2.4"),sQuery(id+"F0.wireOp",EDGE,"E15.2.5"),sQuery(id+"F0.wireOp",EDGE,"E15.2.8"),sQuery(id+"F0.wireOp",EDGE,"E15.2.9"),sQuery(id+"F0.wireOp",EDGE,"E15.2.10"),sQuery(id+"F0.wireOp",EDGE,"E15.2.11"),sQuery(id+"F0.wireOp",EDGE,"E15.2.12"),sQuery(id+"F0.wireOp",EDGE,"E15.2.13"),sQuery(id+"F0.wireOp",EDGE,"E15.2.14"),sQuery(id+"F0.wireOp",EDGE,"E15.2.15"),sQuery(id+"F0.wireOp",EDGE,"E16.1.3.0"),sQuery(id+"F0.wireOp",EDGE,"E16.6.3.0"),sQuery(id+"F0.wireOp",EDGE,"E16.9.3.0"),sQuery(id+"F0.wireOp",EDGE,"E16.12.3.0"),sQuery(id+"F0.wireOp",EDGE,"E16.18.3.0"),sQuery(id+"F0.wireOp",EDGE,"E16.21.3.0"),sQuery(id+"F0.wireOp",EDGE,"E16.24.3.0"),sQuery(id+"F0.wireOp",EDGE,"E16.28.3.0"),sQuery(id+"F0.wireOp",EDGE,"E16.32.3.0"),sQuery(id+"F0.wireOp",EDGE,"E16.36.3.0"),sQuery(id+"F0.wireOp",EDGE,"E16.40.3.0"),sQuery(id+"F0.wireOp",EDGE,"E16.44.3.0"),sQuery(id+"F0.wireOp",EDGE,"E16.1.4.0"),sQuery(id+"F0.wireOp",EDGE,"E16.6.4.0"),sQuery(id+"F0.wireOp",EDGE,"E16.9.4.0"),sQuery(id+"F0.wireOp",EDGE,"E16.12.4.0"),sQuery(id+"F0.wireOp",EDGE,"E16.18.4.0"),sQuery(id+"F0.wireOp",EDGE,"E16.21.4.0"),sQuery(id+"F0.wireOp",EDGE,"E16.24.4.0"),sQuery(id+"F0.wireOp",EDGE,"E16.28.4.0"),sQuery(id+"F0.wireOp",EDGE,"E16.32.4.0"),sQuery(id+"F0.wireOp",EDGE,"E16.36.4.0"),sQuery(id+"F0.wireOp",EDGE,"E16.40.4.0"),sQuery(id+"F0.wireOp",EDGE,"E16.44.4.0"),sQuery(id+"F0.wireOp",EDGE,"E16.1.5.0"),sQuery(id+"F0.wireOp",EDGE,"E16.6.5.0"),sQuery(id+"F0.wireOp",EDGE,"E16.9.5.0"),sQuery(id+"F0.wireOp",EDGE,"E16.12.5.0"),sQuery(id+"F0.wireOp",EDGE,"E16.18.5.0"),sQuery(id+"F0.wireOp",EDGE,"E16.21.5.0"),sQuery(id+"F0.wireOp",EDGE,"E16.24.5.0"),sQuery(id+"F0.wireOp",EDGE,"E16.28.5.0"),sQuery(id+"F0.wireOp",EDGE,"E16.32.5.0"),sQuery(id+"F0.wireOp",EDGE,"E16.36.5.0"),sQuery(id+"F0.wireOp",EDGE,"E16.40.5.0"),sQuery(id+"F0.wireOp",EDGE,"E16.44.5.0"),sQuery(id+"F0.wireOp",EDGE,"E16.1.6.0"),sQuery(id+"F0.wireOp",EDGE,"E16.6.6.0"),sQuery(id+"F0.wireOp",EDGE,"E16.9.6.0"),sQuery(id+"F0.wireOp",EDGE,"E16.12.6.0"),sQuery(id+"F0.wireOp",EDGE,"E16.18.6.0"),sQuery(id+"F0.wireOp",EDGE,"E16.21.6.0"),sQuery(id+"F0.wireOp",EDGE,"E16.24.6.0"),sQuery(id+"F0.wireOp",EDGE,"E16.28.6.0"),sQuery(id+"F0.wireOp",EDGE,"E16.32.6.0"),sQuery(id+"F0.wireOp",EDGE,"E16.36.6.0"),sQuery(id+"F0.wireOp",EDGE,"E16.40.6.0"),sQuery(id+"F0.wireOp",EDGE,"E16.44.6.0"),sQuery(id+"F0.wireOp",EDGE,"E16.1.7.0"),sQuery(id+"F0.wireOp",EDGE,"E16.6.7.0"),sQuery(id+"F0.wireOp",EDGE,"E16.9.7.0"),sQuery(id+"F0.wireOp",EDGE,"E16.12.7.0"),sQuery(id+"F0.wireOp",EDGE,"E16.18.7.0"),sQuery(id+"F0.wireOp",EDGE,"E16.21.7.0"),sQuery(id+"F0.wireOp",EDGE,"E16.24.7.0"),sQuery(id+"F0.wireOp",EDGE,"E16.28.7.0"),sQuery(id+"F0.wireOp",EDGE,"E16.32.7.0"),sQuery(id+"F0.wireOp",EDGE,"E16.36.7.0"),sQuery(id+"F0.wireOp",EDGE,"E16.40.7.0"),sQuery(id+"F0.wireOp",EDGE,"E16.44.7.0"),sQuery(id+"F0.wireOp",EDGE,"E16.1.8.0"),sQuery(id+"F0.wireOp",EDGE,"E16.6.8.0"),sQuery(id+"F0.wireOp",EDGE,"E16.9.8.0"),sQuery(id+"F0.wireOp",EDGE,"E16.12.8.0"),sQuery(id+"F0.wireOp",EDGE,"E16.18.8.0"),sQuery(id+"F0.wireOp",EDGE,"E16.21.8.0"),sQuery(id+"F0.wireOp",EDGE,"E16.24.8.0"),sQuery(id+"F0.wireOp",EDGE,"E16.28.8.0"),sQuery(id+"F0.wireOp",EDGE,"E16.32.8.0"),sQuery(id+"F0.wireOp",EDGE,"E16.36.8.0"),sQuery(id+"F0.wireOp",EDGE,"E16.40.8.0"),sQuery(id+"F0.wireOp",EDGE,"E16.44.8.0"),sQuery(id+"F0.wireOp",EDGE,"E16.1.9.0"),sQuery(id+"F0.wireOp",EDGE,"E16.6.9.0"),sQuery(id+"F0.wireOp",EDGE,"E16.9.9.0"),sQuery(id+"F0.wireOp",EDGE,"E16.12.9.0"),sQuery(id+"F0.wireOp",EDGE,"E16.18.9.0"),sQuery(id+"F0.wireOp",EDGE,"E16.21.9.0"),sQuery(id+"F0.wireOp",EDGE,"E16.24.9.0"),sQuery(id+"F0.wireOp",EDGE,"E16.28.9.0"),sQuery(id+"F0.wireOp",EDGE,"E16.32.9.0"),sQuery(id+"F0.wireOp",EDGE,"E16.36.9.0"),sQuery(id+"F0.wireOp",EDGE,"E16.40.9.0"),sQuery(id+"F0.wireOp",EDGE,"E16.44.9.0"),sQuery(id+"F0.wireOp",EDGE,"E16.1.10.0"),sQuery(id+"F0.wireOp",EDGE,"E16.6.10.0"),sQuery(id+"F0.wireOp",EDGE,"E16.9.10.0"),sQuery(id+"F0.wireOp",EDGE,"E16.12.10.0"),sQuery(id+"F0.wireOp",EDGE,"E16.18.10.0"),sQuery(id+"F0.wireOp",EDGE,"E16.21.10.0"),sQuery(id+"F0.wireOp",EDGE,"E16.24.10.0"),sQuery(id+"F0.wireOp",EDGE,"E16.28.10.0"),sQuery(id+"F0.wireOp",EDGE,"E16.32.10.0"),sQuery(id+"F0.wireOp",EDGE,"E16.36.10.0"),sQuery(id+"F0.wireOp",EDGE,"E16.40.10.0"),sQuery(id+"F0.wireOp",EDGE,"E16.44.10.0"),sQuery(id+"F0.wireOp",EDGE,"E16.1.11.0"),sQuery(id+"F0.wireOp",EDGE,"E16.6.11.0"),sQuery(id+"F0.wireOp",EDGE,"E16.9.11.0"),sQuery(id+"F0.wireOp",EDGE,"E16.12.11.0"),sQuery(id+"F0.wireOp",EDGE,"E16.18.11.0"),sQuery(id+"F0.wireOp",EDGE,"E16.21.11.0"),sQuery(id+"F0.wireOp",EDGE,"E16.24.11.0"),sQuery(id+"F0.wireOp",EDGE,"E16.28.11.0"),sQuery(id+"F0.wireOp",EDGE,"E16.32.11.0"),sQuery(id+"F0.wireOp",EDGE,"E16.36.11.0"),sQuery(id+"F0.wireOp",EDGE,"E16.40.11.0"),sQuery(id+"F0.wireOp",EDGE,"E16.44.11.0"),sQuery(id+"F0.wireOp",EDGE,"E16.1.12.0"),sQuery(id+"F0.wireOp",EDGE,"E16.6.12.0"),sQuery(id+"F0.wireOp",EDGE,"E16.9.12.0"),sQuery(id+"F0.wireOp",EDGE,"E16.12.12.0"),sQuery(id+"F0.wireOp",EDGE,"E16.18.12.0"),sQuery(id+"F0.wireOp",EDGE,"E16.21.12.0"),sQuery(id+"F0.wireOp",EDGE,"E16.24.12.0"),sQuery(id+"F0.wireOp",EDGE,"E16.28.12.0"),sQuery(id+"F0.wireOp",EDGE,"E16.32.12.0"),sQuery(id+"F0.wireOp",EDGE,"E16.36.12.0"),sQuery(id+"F0.wireOp",EDGE,"E16.40.12.0"),sQuery(id+"F0.wireOp",EDGE,"E16.44.12.0"),sQuery(id+"F0.wireOp",EDGE,"E16.1.13.0"),sQuery(id+"F0.wireOp",EDGE,"E16.6.13.0"),sQuery(id+"F0.wireOp",EDGE,"E16.9.13.0"),sQuery(id+"F0.wireOp",EDGE,"E16.12.13.0"),sQuery(id+"F0.wireOp",EDGE,"E16.18.13.0"),sQuery(id+"F0.wireOp",EDGE,"E16.21.13.0"),sQuery(id+"F0.wireOp",EDGE,"E16.24.13.0"),sQuery(id+"F0.wireOp",EDGE,"E16.28.13.0"),sQuery(id+"F0.wireOp",EDGE,"E16.32.13.0"),sQuery(id+"F0.wireOp",EDGE,"E16.36.13.0"),sQuery(id+"F0.wireOp",EDGE,"E16.40.13.0"),sQuery(id+"F0.wireOp",EDGE,"E16.44.13.0"),sQuery(id+"F0.wireOp",EDGE,"E16.1.14.0"),sQuery(id+"F0.wireOp",EDGE,"E16.6.14.0"),sQuery(id+"F0.wireOp",EDGE,"E16.9.14.0"),sQuery(id+"F0.wireOp",EDGE,"E16.12.14.0"),sQuery(id+"F0.wireOp",EDGE,"E16.18.14.0"),sQuery(id+"F0.wireOp",EDGE,"E16.21.14.0"),sQuery(id+"F0.wireOp",EDGE,"E16.24.14.0"),sQuery(id+"F0.wireOp",EDGE,"E16.28.14.0"),sQuery(id+"F0.wireOp",EDGE,"E16.32.14.0"),sQuery(id+"F0.wireOp",EDGE,"E16.36.14.0"),sQuery(id+"F0.wireOp",EDGE,"E16.40.14.0"),sQuery(id+"F0.wireOp",EDGE,"E16.44.14.0"),sQuery(id+"F0.wireOp",EDGE,"E16.1.15.0"),sQuery(id+"F0.wireOp",EDGE,"E16.6.15.0"),sQuery(id+"F0.wireOp",EDGE,"E16.9.15.0"),sQuery(id+"F0.wireOp",EDGE,"E16.12.15.0"),sQuery(id+"F0.wireOp",EDGE,"E16.18.15.0"),sQuery(id+"F0.wireOp",EDGE,"E16.21.15.0"),sQuery(id+"F0.wireOp",EDGE,"E16.24.15.0"),sQuery(id+"F0.wireOp",EDGE,"E16.28.15.0"),sQuery(id+"F0.wireOp",EDGE,"E16.32.15.0"),sQuery(id+"F0.wireOp",EDGE,"E16.36.15.0"),sQuery(id+"F0.wireOp",EDGE,"E16.40.15.0"),sQuery(id+"F0.wireOp",EDGE,"E16.44.15.0"),sQuery(id+"F0.wireOp",EDGE,"E16.1.16.0"),sQuery(id+"F0.wireOp",EDGE,"E16.6.16.0"),sQuery(id+"F0.wireOp",EDGE,"E16.9.16.0"),sQuery(id+"F0.wireOp",EDGE,"E16.12.16.0"),sQuery(id+"F0.wireOp",EDGE,"E16.18.16.0"),sQuery(id+"F0.wireOp",EDGE,"E16.21.16.0"),sQuery(id+"F0.wireOp",EDGE,"E16.24.16.0"),sQuery(id+"F0.wireOp",EDGE,"E16.28.16.0"),sQuery(id+"F0.wireOp",EDGE,"E16.32.16.0"),sQuery(id+"F0.wireOp",EDGE,"E16.36.16.0"),sQuery(id+"F0.wireOp",EDGE,"E16.40.16.0"),sQuery(id+"F0.wireOp",EDGE,"E16.44.16.0"),sQuery(id+"F0.wireOp",EDGE,"E16.1.17.0"),sQuery(id+"F0.wireOp",EDGE,"E16.6.17.0"),sQuery(id+"F0.wireOp",EDGE,"E16.9.17.0"),sQuery(id+"F0.wireOp",EDGE,"E16.12.17.0"),sQuery(id+"F0.wireOp",EDGE,"E16.18.17.0"),sQuery(id+"F0.wireOp",EDGE,"E16.21.17.0"),sQuery(id+"F0.wireOp",EDGE,"E16.24.17.0"),sQuery(id+"F0.wireOp",EDGE,"E16.28.17.0"),sQuery(id+"F0.wireOp",EDGE,"E16.32.17.0"),sQuery(id+"F0.wireOp",EDGE,"E16.36.17.0"),sQuery(id+"F0.wireOp",EDGE,"E16.40.17.0"),sQuery(id+"F0.wireOp",EDGE,"E16.44.17.0"),sQuery(id+"F0.wireOp",EDGE,"E16.1.18.0"),sQuery(id+"F0.wireOp",EDGE,"E16.6.18.0"),sQuery(id+"F0.wireOp",EDGE,"E16.9.18.0"),sQuery(id+"F0.wireOp",EDGE,"E16.12.18.0"),sQuery(id+"F0.wireOp",EDGE,"E16.18.18.0"),sQuery(id+"F0.wireOp",EDGE,"E16.21.18.0"),sQuery(id+"F0.wireOp",EDGE,"E16.24.18.0"),sQuery(id+"F0.wireOp",EDGE,"E16.28.18.0"),sQuery(id+"F0.wireOp",EDGE,"E16.32.18.0"),sQuery(id+"F0.wireOp",EDGE,"E16.36.18.0"),sQuery(id+"F0.wireOp",EDGE,"E16.40.18.0"),sQuery(id+"F0.wireOp",EDGE,"E16.44.18.0"),sQuery(id+"F0.wireOp",EDGE,"E16.1.19.0"),sQuery(id+"F0.wireOp",EDGE,"E16.6.19.0"),sQuery(id+"F0.wireOp",EDGE,"E16.9.19.0"),sQuery(id+"F0.wireOp",EDGE,"E16.12.19.0"),sQuery(id+"F0.wireOp",EDGE,"E16.18.19.0"),sQuery(id+"F0.wireOp",EDGE,"E16.21.19.0"),sQuery(id+"F0.wireOp",EDGE,"E16.24.19.0"),sQuery(id+"F0.wireOp",EDGE,"E16.28.19.0"),sQuery(id+"F0.wireOp",EDGE,"E16.32.19.0"),sQuery(id+"F0.wireOp",EDGE,"E16.36.19.0"),sQuery(id+"F0.wireOp",EDGE,"E16.40.19.0"),sQuery(id+"F0.wireOp",EDGE,"E16.44.19.0"),sQuery(id+"F0.wireOp",EDGE,"E16.1.20.0"),sQuery(id+"F0.wireOp",EDGE,"E16.6.20.0"),sQuery(id+"F0.wireOp",EDGE,"E16.9.20.0"),sQuery(id+"F0.wireOp",EDGE,"E16.12.20.0"),sQuery(id+"F0.wireOp",EDGE,"E16.18.20.0"),sQuery(id+"F0.wireOp",EDGE,"E16.21.20.0"),sQuery(id+"F0.wireOp",EDGE,"E16.24.20.0"),sQuery(id+"F0.wireOp",EDGE,"E16.28.20.0"),sQuery(id+"F0.wireOp",EDGE,"E16.32.20.0"),sQuery(id+"F0.wireOp",EDGE,"E16.36.20.0"),sQuery(id+"F0.wireOp",EDGE,"E16.40.20.0"),sQuery(id+"F0.wireOp",EDGE,"E16.44.20.0"),sQuery(id+"F0.wireOp",EDGE,"E16.1.21.0"),sQuery(id+"F0.wireOp",EDGE,"E16.6.21.0"),sQuery(id+"F0.wireOp",EDGE,"E16.9.21.0"),sQuery(id+"F0.wireOp",EDGE,"E16.12.21.0"),sQuery(id+"F0.wireOp",EDGE,"E16.18.21.0"),sQuery(id+"F0.wireOp",EDGE,"E16.21.21.0"),sQuery(id+"F0.wireOp",EDGE,"E16.24.21.0"),sQuery(id+"F0.wireOp",EDGE,"E16.28.21.0"),sQuery(id+"F0.wireOp",EDGE,"E16.32.21.0"),sQuery(id+"F0.wireOp",EDGE,"E16.36.21.0"),sQuery(id+"F0.wireOp",EDGE,"E16.40.21.0"),sQuery(id+"F0.wireOp",EDGE,"E16.44.21.0"),sQuery(id+"F0.wireOp",EDGE,"E16.1.22.0"),sQuery(id+"F0.wireOp",EDGE,"E16.6.22.0"),sQuery(id+"F0.wireOp",EDGE,"E16.9.22.0"),sQuery(id+"F0.wireOp",EDGE,"E16.12.22.0"),sQuery(id+"F0.wireOp",EDGE,"E16.18.22.0"),sQuery(id+"F0.wireOp",EDGE,"E16.21.22.0"),sQuery(id+"F0.wireOp",EDGE,"E16.24.22.0"),sQuery(id+"F0.wireOp",EDGE,"E16.28.22.0"),sQuery(id+"F0.wireOp",EDGE,"E16.32.22.0"),sQuery(id+"F0.wireOp",EDGE,"E16.36.22.0"),sQuery(id+"F0.wireOp",EDGE,"E16.40.22.0"),sQuery(id+"F0.wireOp",EDGE,"E16.44.22.0"),sQuery(id+"F0.wireOp",EDGE,"E16.1.23.0"),sQuery(id+"F0.wireOp",EDGE,"E16.6.23.0"),sQuery(id+"F0.wireOp",EDGE,"E16.9.23.0"),sQuery(id+"F0.wireOp",EDGE,"E16.12.23.0"),sQuery(id+"F0.wireOp",EDGE,"E16.18.23.0"),sQuery(id+"F0.wireOp",EDGE,"E16.21.23.0"),sQuery(id+"F0.wireOp",EDGE,"E16.24.23.0"),sQuery(id+"F0.wireOp",EDGE,"E16.28.23.0"),sQuery(id+"F0.wireOp",EDGE,"E16.32.23.0"),sQuery(id+"F0.wireOp",EDGE,"E16.36.23.0"),sQuery(id+"F0.wireOp",EDGE,"E16.40.23.0"),sQuery(id+"F0.wireOp",EDGE,"E16.44.23.0"),sQuery(id+"F0.wireOp",EDGE,"E16.1.24.0"),sQuery(id+"F0.wireOp",EDGE,"E16.6.24.0"),sQuery(id+"F0.wireOp",EDGE,"E16.9.24.0"),sQuery(id+"F0.wireOp",EDGE,"E16.12.24.0"),sQuery(id+"F0.wireOp",EDGE,"E16.18.24.0"),sQuery(id+"F0.wireOp",EDGE,"E16.21.24.0"),sQuery(id+"F0.wireOp",EDGE,"E16.24.24.0"),sQuery(id+"F0.wireOp",EDGE,"E16.28.24.0"),sQuery(id+"F0.wireOp",EDGE,"E16.32.24.0"),sQuery(id+"F0.wireOp",EDGE,"E16.36.24.0"),sQuery(id+"F0.wireOp",EDGE,"E16.40.24.0"),sQuery(id+"F0.wireOp",EDGE,"E16.44.24.0"),sQuery(id+"F0.wireOp",EDGE,"E16.1.25.0"),sQuery(id+"F0.wireOp",EDGE,"E16.6.25.0"),sQuery(id+"F0.wireOp",EDGE,"E16.9.25.0"),sQuery(id+"F0.wireOp",EDGE,"E16.12.25.0"),sQuery(id+"F0.wireOp",EDGE,"E16.18.25.0"),sQuery(id+"F0.wireOp",EDGE,"E16.21.25.0"),sQuery(id+"F0.wireOp",EDGE,"E16.24.25.0"),sQuery(id+"F0.wireOp",EDGE,"E16.28.25.0"),sQuery(id+"F0.wireOp",EDGE,"E16.32.25.0"),sQuery(id+"F0.wireOp",EDGE,"E16.36.25.0"),sQuery(id+"F0.wireOp",EDGE,"E16.40.25.0"),sQuery(id+"F0.wireOp",EDGE,"E16.44.25.0"),sQuery(id+"F0.wireOp",EDGE,"E16.1.26.0"),sQuery(id+"F0.wireOp",EDGE,"E16.6.26.0"),sQuery(id+"F0.wireOp",EDGE,"E16.9.26.0"),sQuery(id+"F0.wireOp",EDGE,"E16.12.26.0"),sQuery(id+"F0.wireOp",EDGE,"E16.18.26.0"),sQuery(id+"F0.wireOp",EDGE,"E16.21.26.0"),sQuery(id+"F0.wireOp",EDGE,"E16.24.26.0"),sQuery(id+"F0.wireOp",EDGE,"E16.28.26.0"),sQuery(id+"F0.wireOp",EDGE,"E16.32.26.0"),sQuery(id+"F0.wireOp",EDGE,"E16.36.26.0"),sQuery(id+"F0.wireOp",EDGE,"E16.40.26.0"),sQuery(id+"F0.wireOp",EDGE,"E16.44.26.0"),sQuery(id+"F0.wireOp",EDGE,"E16.1.27.0"),sQuery(id+"F0.wireOp",EDGE,"E16.6.27.0"),sQuery(id+"F0.wireOp",EDGE,"E16.9.27.0"),sQuery(id+"F0.wireOp",EDGE,"E16.12.27.0"),sQuery(id+"F0.wireOp",EDGE,"E16.18.27.0"),sQuery(id+"F0.wireOp",EDGE,"E16.21.27.0"),sQuery(id+"F0.wireOp",EDGE,"E16.24.27.0"),sQuery(id+"F0.wireOp",EDGE,"E16.28.27.0"),sQuery(id+"F0.wireOp",EDGE,"E16.32.27.0"),sQuery(id+"F0.wireOp",EDGE,"E16.36.27.0"),sQuery(id+"F0.wireOp",EDGE,"E16.40.27.0"),sQuery(id+"F0.wireOp",EDGE,"E16.44.27.0"),sQuery(id+"F0.wireOp",EDGE,"E17.trimOffspring"),sQuery(id+"F0.wireOp",EDGE,"E18.trimOffspring"),sQuery(id+"F0.wireOp",EDGE,"E19.trimOffspring"),sQuery(id+"F0.wireOp",EDGE,"E20.trimOffspring"),sQuery(id+"F0.wireOp",EDGE,"E21.trimOffspring"),sQuery(id+"F0.wireOp",EDGE,"E22.trimOffspring"),sQuery(id+"F0.wireOp",EDGE,"E23.trimOffspring"),sQuery(id+"F0.wireOp",EDGE,"E24.trimOffspring"),sQuery(id+"F0.wireOp",EDGE,"E25.trimOffspring"),sQuery(id+"F0.wireOp",EDGE,"E26.trimOffspring"),sQuery(id+"F0.wireOp",EDGE,"E27.trimOffspring"),sQuery(id+"F0.wireOp",EDGE,"E28.trimOffspring"),sQuery(id+"F0.wireOp",EDGE,"E29.trimOffspring"),sQuery(id+"F0.wireOp",EDGE,"E30.trimOffspring"),sQuery(id+"F0.wireOp",EDGE,"E31.trimOffspring"),sQuery(id+"F0.wireOp",EDGE,"E32.trimOffspring"),sQuery(id+"F0.wireOp",EDGE,"E33.trimOffspring"),sQuery(id+"F0.wireOp",EDGE,"E34.trimOffspring"),sQuery(id+"F0.wireOp",EDGE,"E35.trimOffspring"),sQuery(id+"F0.wireOp",EDGE,"E36.trimOffspring"),sQuery(id+"F0.wireOp",EDGE,"E37.trimOffspring"),sQuery(id+"F0.wireOp",EDGE,"E38.trimOffspring"),sQuery(id+"F0.wireOp",EDGE,"E39.trimOffspring"),sQuery(id+"F0.wireOp",EDGE,"E40.trimOffspring"),sQuery(id+"F0.wireOp",EDGE,"E41.trimOffspring"),sQuery(id+"F0.wireOp",EDGE,"E42.trimOffspring"),sQuery(id+"F0.wireOp",EDGE,"E43.trimOffspring")])]});
            hole(context, id + "F5", {"style" : HoleStyle.SIMPLE, "endStyle" : HoleEndStyle.THROUGH, "holeDiameter" : 7.87 * mm, "locations" : qUnion([Q0]), "scope" : qUnion([Q1]), "isTappedThrough" : true});
        }
        {
            var Q0;
            Q0=makeQuery(id+"F1.opExtrude","CAP_FACE",FACE,{"disambiguationData":[OSD([sQuery(id+"F0.wireOp",EDGE,"E0"),sQuery(id+"F0.wireOp",EDGE,"E1.trimOffspring"),sQuery(id+"F0.wireOp",EDGE,"E2"),sQuery(id+"F0.wireOp",EDGE,"E3"),sQuery(id+"F0.wireOp",EDGE,"E4.MirrorCS"),sQuery(id+"F0.wireOp",EDGE,"E5.MirrorCS"),sQuery(id+"F0.wireOp",EDGE,"E6.MirrorCS"),sQuery(id+"F0.wireOp",EDGE,"E9.filletArc"),sQuery(id+"F0.wireOp",EDGE,"E10.filletArc"),sQuery(id+"F0.wireOp",EDGE,"E11.filletArc"),sQuery(id+"F0.wireOp",EDGE,"E12.filletArc"),sQuery(id+"F0.wireOp",EDGE,"E13.filletArc"),sQuery(id+"F0.wireOp",EDGE,"E14.filletArc"),sQuery(id+"F0.wireOp",EDGE,"E15.1.0"),sQuery(id+"F0.wireOp",EDGE,"E15.1.3"),sQuery(id+"F0.wireOp",EDGE,"E15.1.4"),sQuery(id+"F0.wireOp",EDGE,"E15.1.5"),sQuery(id+"F0.wireOp",EDGE,"E15.1.8"),sQuery(id+"F0.wireOp",EDGE,"E15.1.9"),sQuery(id+"F0.wireOp",EDGE,"E15.1.10"),sQuery(id+"F0.wireOp",EDGE,"E15.1.11"),sQuery(id+"F0.wireOp",EDGE,"E15.1.12"),sQuery(id+"F0.wireOp",EDGE,"E15.1.13"),sQuery(id+"F0.wireOp",EDGE,"E15.1.14"),sQuery(id+"F0.wireOp",EDGE,"E15.1.15"),sQuery(id+"F0.wireOp",EDGE,"E15.2.0"),sQuery(id+"F0.wireOp",EDGE,"E15.2.3"),sQuery(id+"F0.wireOp",EDGE,"E15.2.4"),sQuery(id+"F0.wireOp",EDGE,"E15.2.5"),sQuery(id+"F0.wireOp",EDGE,"E15.2.8"),sQuery(id+"F0.wireOp",EDGE,"E15.2.9"),sQuery(id+"F0.wireOp",EDGE,"E15.2.10"),sQuery(id+"F0.wireOp",EDGE,"E15.2.11"),sQuery(id+"F0.wireOp",EDGE,"E15.2.12"),sQuery(id+"F0.wireOp",EDGE,"E15.2.13"),sQuery(id+"F0.wireOp",EDGE,"E15.2.14"),sQuery(id+"F0.wireOp",EDGE,"E15.2.15"),sQuery(id+"F0.wireOp",EDGE,"E16.1.3.0"),sQuery(id+"F0.wireOp",EDGE,"E16.6.3.0"),sQuery(id+"F0.wireOp",EDGE,"E16.9.3.0"),sQuery(id+"F0.wireOp",EDGE,"E16.12.3.0"),sQuery(id+"F0.wireOp",EDGE,"E16.18.3.0"),sQuery(id+"F0.wireOp",EDGE,"E16.21.3.0"),sQuery(id+"F0.wireOp",EDGE,"E16.24.3.0"),sQuery(id+"F0.wireOp",EDGE,"E16.28.3.0"),sQuery(id+"F0.wireOp",EDGE,"E16.32.3.0"),sQuery(id+"F0.wireOp",EDGE,"E16.36.3.0"),sQuery(id+"F0.wireOp",EDGE,"E16.40.3.0"),sQuery(id+"F0.wireOp",EDGE,"E16.44.3.0"),sQuery(id+"F0.wireOp",EDGE,"E16.1.4.0"),sQuery(id+"F0.wireOp",EDGE,"E16.6.4.0"),sQuery(id+"F0.wireOp",EDGE,"E16.9.4.0"),sQuery(id+"F0.wireOp",EDGE,"E16.12.4.0"),sQuery(id+"F0.wireOp",EDGE,"E16.18.4.0"),sQuery(id+"F0.wireOp",EDGE,"E16.21.4.0"),sQuery(id+"F0.wireOp",EDGE,"E16.24.4.0"),sQuery(id+"F0.wireOp",EDGE,"E16.28.4.0"),sQuery(id+"F0.wireOp",EDGE,"E16.32.4.0"),sQuery(id+"F0.wireOp",EDGE,"E16.36.4.0"),sQuery(id+"F0.wireOp",EDGE,"E16.40.4.0"),sQuery(id+"F0.wireOp",EDGE,"E16.44.4.0"),sQuery(id+"F0.wireOp",EDGE,"E16.1.5.0"),sQuery(id+"F0.wireOp",EDGE,"E16.6.5.0"),sQuery(id+"F0.wireOp",EDGE,"E16.9.5.0"),sQuery(id+"F0.wireOp",EDGE,"E16.12.5.0"),sQuery(id+"F0.wireOp",EDGE,"E16.18.5.0"),sQuery(id+"F0.wireOp",EDGE,"E16.21.5.0"),sQuery(id+"F0.wireOp",EDGE,"E16.24.5.0"),sQuery(id+"F0.wireOp",EDGE,"E16.28.5.0"),sQuery(id+"F0.wireOp",EDGE,"E16.32.5.0"),sQuery(id+"F0.wireOp",EDGE,"E16.36.5.0"),sQuery(id+"F0.wireOp",EDGE,"E16.40.5.0"),sQuery(id+"F0.wireOp",EDGE,"E16.44.5.0"),sQuery(id+"F0.wireOp",EDGE,"E16.1.6.0"),sQuery(id+"F0.wireOp",EDGE,"E16.6.6.0"),sQuery(id+"F0.wireOp",EDGE,"E16.9.6.0"),sQuery(id+"F0.wireOp",EDGE,"E16.12.6.0"),sQuery(id+"F0.wireOp",EDGE,"E16.18.6.0"),sQuery(id+"F0.wireOp",EDGE,"E16.21.6.0"),sQuery(id+"F0.wireOp",EDGE,"E16.24.6.0"),sQuery(id+"F0.wireOp",EDGE,"E16.28.6.0"),sQuery(id+"F0.wireOp",EDGE,"E16.32.6.0"),sQuery(id+"F0.wireOp",EDGE,"E16.36.6.0"),sQuery(id+"F0.wireOp",EDGE,"E16.40.6.0"),sQuery(id+"F0.wireOp",EDGE,"E16.44.6.0"),sQuery(id+"F0.wireOp",EDGE,"E16.1.7.0"),sQuery(id+"F0.wireOp",EDGE,"E16.6.7.0"),sQuery(id+"F0.wireOp",EDGE,"E16.9.7.0"),sQuery(id+"F0.wireOp",EDGE,"E16.12.7.0"),sQuery(id+"F0.wireOp",EDGE,"E16.18.7.0"),sQuery(id+"F0.wireOp",EDGE,"E16.21.7.0"),sQuery(id+"F0.wireOp",EDGE,"E16.24.7.0"),sQuery(id+"F0.wireOp",EDGE,"E16.28.7.0"),sQuery(id+"F0.wireOp",EDGE,"E16.32.7.0"),sQuery(id+"F0.wireOp",EDGE,"E16.36.7.0"),sQuery(id+"F0.wireOp",EDGE,"E16.40.7.0"),sQuery(id+"F0.wireOp",EDGE,"E16.44.7.0"),sQuery(id+"F0.wireOp",EDGE,"E16.1.8.0"),sQuery(id+"F0.wireOp",EDGE,"E16.6.8.0"),sQuery(id+"F0.wireOp",EDGE,"E16.9.8.0"),sQuery(id+"F0.wireOp",EDGE,"E16.12.8.0"),sQuery(id+"F0.wireOp",EDGE,"E16.18.8.0"),sQuery(id+"F0.wireOp",EDGE,"E16.21.8.0"),sQuery(id+"F0.wireOp",EDGE,"E16.24.8.0"),sQuery(id+"F0.wireOp",EDGE,"E16.28.8.0"),sQuery(id+"F0.wireOp",EDGE,"E16.32.8.0"),sQuery(id+"F0.wireOp",EDGE,"E16.36.8.0"),sQuery(id+"F0.wireOp",EDGE,"E16.40.8.0"),sQuery(id+"F0.wireOp",EDGE,"E16.44.8.0"),sQuery(id+"F0.wireOp",EDGE,"E16.1.9.0"),sQuery(id+"F0.wireOp",EDGE,"E16.6.9.0"),sQuery(id+"F0.wireOp",EDGE,"E16.9.9.0"),sQuery(id+"F0.wireOp",EDGE,"E16.12.9.0"),sQuery(id+"F0.wireOp",EDGE,"E16.18.9.0"),sQuery(id+"F0.wireOp",EDGE,"E16.21.9.0"),sQuery(id+"F0.wireOp",EDGE,"E16.24.9.0"),sQuery(id+"F0.wireOp",EDGE,"E16.28.9.0"),sQuery(id+"F0.wireOp",EDGE,"E16.32.9.0"),sQuery(id+"F0.wireOp",EDGE,"E16.36.9.0"),sQuery(id+"F0.wireOp",EDGE,"E16.40.9.0"),sQuery(id+"F0.wireOp",EDGE,"E16.44.9.0"),sQuery(id+"F0.wireOp",EDGE,"E16.1.10.0"),sQuery(id+"F0.wireOp",EDGE,"E16.6.10.0"),sQuery(id+"F0.wireOp",EDGE,"E16.9.10.0"),sQuery(id+"F0.wireOp",EDGE,"E16.12.10.0"),sQuery(id+"F0.wireOp",EDGE,"E16.18.10.0"),sQuery(id+"F0.wireOp",EDGE,"E16.21.10.0"),sQuery(id+"F0.wireOp",EDGE,"E16.24.10.0"),sQuery(id+"F0.wireOp",EDGE,"E16.28.10.0"),sQuery(id+"F0.wireOp",EDGE,"E16.32.10.0"),sQuery(id+"F0.wireOp",EDGE,"E16.36.10.0"),sQuery(id+"F0.wireOp",EDGE,"E16.40.10.0"),sQuery(id+"F0.wireOp",EDGE,"E16.44.10.0"),sQuery(id+"F0.wireOp",EDGE,"E16.1.11.0"),sQuery(id+"F0.wireOp",EDGE,"E16.6.11.0"),sQuery(id+"F0.wireOp",EDGE,"E16.9.11.0"),sQuery(id+"F0.wireOp",EDGE,"E16.12.11.0"),sQuery(id+"F0.wireOp",EDGE,"E16.18.11.0"),sQuery(id+"F0.wireOp",EDGE,"E16.21.11.0"),sQuery(id+"F0.wireOp",EDGE,"E16.24.11.0"),sQuery(id+"F0.wireOp",EDGE,"E16.28.11.0"),sQuery(id+"F0.wireOp",EDGE,"E16.32.11.0"),sQuery(id+"F0.wireOp",EDGE,"E16.36.11.0"),sQuery(id+"F0.wireOp",EDGE,"E16.40.11.0"),sQuery(id+"F0.wireOp",EDGE,"E16.44.11.0"),sQuery(id+"F0.wireOp",EDGE,"E16.1.12.0"),sQuery(id+"F0.wireOp",EDGE,"E16.6.12.0"),sQuery(id+"F0.wireOp",EDGE,"E16.9.12.0"),sQuery(id+"F0.wireOp",EDGE,"E16.12.12.0"),sQuery(id+"F0.wireOp",EDGE,"E16.18.12.0"),sQuery(id+"F0.wireOp",EDGE,"E16.21.12.0"),sQuery(id+"F0.wireOp",EDGE,"E16.24.12.0"),sQuery(id+"F0.wireOp",EDGE,"E16.28.12.0"),sQuery(id+"F0.wireOp",EDGE,"E16.32.12.0"),sQuery(id+"F0.wireOp",EDGE,"E16.36.12.0"),sQuery(id+"F0.wireOp",EDGE,"E16.40.12.0"),sQuery(id+"F0.wireOp",EDGE,"E16.44.12.0"),sQuery(id+"F0.wireOp",EDGE,"E16.1.13.0"),sQuery(id+"F0.wireOp",EDGE,"E16.6.13.0"),sQuery(id+"F0.wireOp",EDGE,"E16.9.13.0"),sQuery(id+"F0.wireOp",EDGE,"E16.12.13.0"),sQuery(id+"F0.wireOp",EDGE,"E16.18.13.0"),sQuery(id+"F0.wireOp",EDGE,"E16.21.13.0"),sQuery(id+"F0.wireOp",EDGE,"E16.24.13.0"),sQuery(id+"F0.wireOp",EDGE,"E16.28.13.0"),sQuery(id+"F0.wireOp",EDGE,"E16.32.13.0"),sQuery(id+"F0.wireOp",EDGE,"E16.36.13.0"),sQuery(id+"F0.wireOp",EDGE,"E16.40.13.0"),sQuery(id+"F0.wireOp",EDGE,"E16.44.13.0"),sQuery(id+"F0.wireOp",EDGE,"E16.1.14.0"),sQuery(id+"F0.wireOp",EDGE,"E16.6.14.0"),sQuery(id+"F0.wireOp",EDGE,"E16.9.14.0"),sQuery(id+"F0.wireOp",EDGE,"E16.12.14.0"),sQuery(id+"F0.wireOp",EDGE,"E16.18.14.0"),sQuery(id+"F0.wireOp",EDGE,"E16.21.14.0"),sQuery(id+"F0.wireOp",EDGE,"E16.24.14.0"),sQuery(id+"F0.wireOp",EDGE,"E16.28.14.0"),sQuery(id+"F0.wireOp",EDGE,"E16.32.14.0"),sQuery(id+"F0.wireOp",EDGE,"E16.36.14.0"),sQuery(id+"F0.wireOp",EDGE,"E16.40.14.0"),sQuery(id+"F0.wireOp",EDGE,"E16.44.14.0"),sQuery(id+"F0.wireOp",EDGE,"E16.1.15.0"),sQuery(id+"F0.wireOp",EDGE,"E16.6.15.0"),sQuery(id+"F0.wireOp",EDGE,"E16.9.15.0"),sQuery(id+"F0.wireOp",EDGE,"E16.12.15.0"),sQuery(id+"F0.wireOp",EDGE,"E16.18.15.0"),sQuery(id+"F0.wireOp",EDGE,"E16.21.15.0"),sQuery(id+"F0.wireOp",EDGE,"E16.24.15.0"),sQuery(id+"F0.wireOp",EDGE,"E16.28.15.0"),sQuery(id+"F0.wireOp",EDGE,"E16.32.15.0"),sQuery(id+"F0.wireOp",EDGE,"E16.36.15.0"),sQuery(id+"F0.wireOp",EDGE,"E16.40.15.0"),sQuery(id+"F0.wireOp",EDGE,"E16.44.15.0"),sQuery(id+"F0.wireOp",EDGE,"E16.1.16.0"),sQuery(id+"F0.wireOp",EDGE,"E16.6.16.0"),sQuery(id+"F0.wireOp",EDGE,"E16.9.16.0"),sQuery(id+"F0.wireOp",EDGE,"E16.12.16.0"),sQuery(id+"F0.wireOp",EDGE,"E16.18.16.0"),sQuery(id+"F0.wireOp",EDGE,"E16.21.16.0"),sQuery(id+"F0.wireOp",EDGE,"E16.24.16.0"),sQuery(id+"F0.wireOp",EDGE,"E16.28.16.0"),sQuery(id+"F0.wireOp",EDGE,"E16.32.16.0"),sQuery(id+"F0.wireOp",EDGE,"E16.36.16.0"),sQuery(id+"F0.wireOp",EDGE,"E16.40.16.0"),sQuery(id+"F0.wireOp",EDGE,"E16.44.16.0"),sQuery(id+"F0.wireOp",EDGE,"E16.1.17.0"),sQuery(id+"F0.wireOp",EDGE,"E16.6.17.0"),sQuery(id+"F0.wireOp",EDGE,"E16.9.17.0"),sQuery(id+"F0.wireOp",EDGE,"E16.12.17.0"),sQuery(id+"F0.wireOp",EDGE,"E16.18.17.0"),sQuery(id+"F0.wireOp",EDGE,"E16.21.17.0"),sQuery(id+"F0.wireOp",EDGE,"E16.24.17.0"),sQuery(id+"F0.wireOp",EDGE,"E16.28.17.0"),sQuery(id+"F0.wireOp",EDGE,"E16.32.17.0"),sQuery(id+"F0.wireOp",EDGE,"E16.36.17.0"),sQuery(id+"F0.wireOp",EDGE,"E16.40.17.0"),sQuery(id+"F0.wireOp",EDGE,"E16.44.17.0"),sQuery(id+"F0.wireOp",EDGE,"E16.1.18.0"),sQuery(id+"F0.wireOp",EDGE,"E16.6.18.0"),sQuery(id+"F0.wireOp",EDGE,"E16.9.18.0"),sQuery(id+"F0.wireOp",EDGE,"E16.12.18.0"),sQuery(id+"F0.wireOp",EDGE,"E16.18.18.0"),sQuery(id+"F0.wireOp",EDGE,"E16.21.18.0"),sQuery(id+"F0.wireOp",EDGE,"E16.24.18.0"),sQuery(id+"F0.wireOp",EDGE,"E16.28.18.0"),sQuery(id+"F0.wireOp",EDGE,"E16.32.18.0"),sQuery(id+"F0.wireOp",EDGE,"E16.36.18.0"),sQuery(id+"F0.wireOp",EDGE,"E16.40.18.0"),sQuery(id+"F0.wireOp",EDGE,"E16.44.18.0"),sQuery(id+"F0.wireOp",EDGE,"E16.1.19.0"),sQuery(id+"F0.wireOp",EDGE,"E16.6.19.0"),sQuery(id+"F0.wireOp",EDGE,"E16.9.19.0"),sQuery(id+"F0.wireOp",EDGE,"E16.12.19.0"),sQuery(id+"F0.wireOp",EDGE,"E16.18.19.0"),sQuery(id+"F0.wireOp",EDGE,"E16.21.19.0"),sQuery(id+"F0.wireOp",EDGE,"E16.24.19.0"),sQuery(id+"F0.wireOp",EDGE,"E16.28.19.0"),sQuery(id+"F0.wireOp",EDGE,"E16.32.19.0"),sQuery(id+"F0.wireOp",EDGE,"E16.36.19.0"),sQuery(id+"F0.wireOp",EDGE,"E16.40.19.0"),sQuery(id+"F0.wireOp",EDGE,"E16.44.19.0"),sQuery(id+"F0.wireOp",EDGE,"E16.1.20.0"),sQuery(id+"F0.wireOp",EDGE,"E16.6.20.0"),sQuery(id+"F0.wireOp",EDGE,"E16.9.20.0"),sQuery(id+"F0.wireOp",EDGE,"E16.12.20.0"),sQuery(id+"F0.wireOp",EDGE,"E16.18.20.0"),sQuery(id+"F0.wireOp",EDGE,"E16.21.20.0"),sQuery(id+"F0.wireOp",EDGE,"E16.24.20.0"),sQuery(id+"F0.wireOp",EDGE,"E16.28.20.0"),sQuery(id+"F0.wireOp",EDGE,"E16.32.20.0"),sQuery(id+"F0.wireOp",EDGE,"E16.36.20.0"),sQuery(id+"F0.wireOp",EDGE,"E16.40.20.0"),sQuery(id+"F0.wireOp",EDGE,"E16.44.20.0"),sQuery(id+"F0.wireOp",EDGE,"E16.1.21.0"),sQuery(id+"F0.wireOp",EDGE,"E16.6.21.0"),sQuery(id+"F0.wireOp",EDGE,"E16.9.21.0"),sQuery(id+"F0.wireOp",EDGE,"E16.12.21.0"),sQuery(id+"F0.wireOp",EDGE,"E16.18.21.0"),sQuery(id+"F0.wireOp",EDGE,"E16.21.21.0"),sQuery(id+"F0.wireOp",EDGE,"E16.24.21.0"),sQuery(id+"F0.wireOp",EDGE,"E16.28.21.0"),sQuery(id+"F0.wireOp",EDGE,"E16.32.21.0"),sQuery(id+"F0.wireOp",EDGE,"E16.36.21.0"),sQuery(id+"F0.wireOp",EDGE,"E16.40.21.0"),sQuery(id+"F0.wireOp",EDGE,"E16.44.21.0"),sQuery(id+"F0.wireOp",EDGE,"E16.1.22.0"),sQuery(id+"F0.wireOp",EDGE,"E16.6.22.0"),sQuery(id+"F0.wireOp",EDGE,"E16.9.22.0"),sQuery(id+"F0.wireOp",EDGE,"E16.12.22.0"),sQuery(id+"F0.wireOp",EDGE,"E16.18.22.0"),sQuery(id+"F0.wireOp",EDGE,"E16.21.22.0"),sQuery(id+"F0.wireOp",EDGE,"E16.24.22.0"),sQuery(id+"F0.wireOp",EDGE,"E16.28.22.0"),sQuery(id+"F0.wireOp",EDGE,"E16.32.22.0"),sQuery(id+"F0.wireOp",EDGE,"E16.36.22.0"),sQuery(id+"F0.wireOp",EDGE,"E16.40.22.0"),sQuery(id+"F0.wireOp",EDGE,"E16.44.22.0"),sQuery(id+"F0.wireOp",EDGE,"E16.1.23.0"),sQuery(id+"F0.wireOp",EDGE,"E16.6.23.0"),sQuery(id+"F0.wireOp",EDGE,"E16.9.23.0"),sQuery(id+"F0.wireOp",EDGE,"E16.12.23.0"),sQuery(id+"F0.wireOp",EDGE,"E16.18.23.0"),sQuery(id+"F0.wireOp",EDGE,"E16.21.23.0"),sQuery(id+"F0.wireOp",EDGE,"E16.24.23.0"),sQuery(id+"F0.wireOp",EDGE,"E16.28.23.0"),sQuery(id+"F0.wireOp",EDGE,"E16.32.23.0"),sQuery(id+"F0.wireOp",EDGE,"E16.36.23.0"),sQuery(id+"F0.wireOp",EDGE,"E16.40.23.0"),sQuery(id+"F0.wireOp",EDGE,"E16.44.23.0"),sQuery(id+"F0.wireOp",EDGE,"E16.1.24.0"),sQuery(id+"F0.wireOp",EDGE,"E16.6.24.0"),sQuery(id+"F0.wireOp",EDGE,"E16.9.24.0"),sQuery(id+"F0.wireOp",EDGE,"E16.12.24.0"),sQuery(id+"F0.wireOp",EDGE,"E16.18.24.0"),sQuery(id+"F0.wireOp",EDGE,"E16.21.24.0"),sQuery(id+"F0.wireOp",EDGE,"E16.24.24.0"),sQuery(id+"F0.wireOp",EDGE,"E16.28.24.0"),sQuery(id+"F0.wireOp",EDGE,"E16.32.24.0"),sQuery(id+"F0.wireOp",EDGE,"E16.36.24.0"),sQuery(id+"F0.wireOp",EDGE,"E16.40.24.0"),sQuery(id+"F0.wireOp",EDGE,"E16.44.24.0"),sQuery(id+"F0.wireOp",EDGE,"E16.1.25.0"),sQuery(id+"F0.wireOp",EDGE,"E16.6.25.0"),sQuery(id+"F0.wireOp",EDGE,"E16.9.25.0"),sQuery(id+"F0.wireOp",EDGE,"E16.12.25.0"),sQuery(id+"F0.wireOp",EDGE,"E16.18.25.0"),sQuery(id+"F0.wireOp",EDGE,"E16.21.25.0"),sQuery(id+"F0.wireOp",EDGE,"E16.24.25.0"),sQuery(id+"F0.wireOp",EDGE,"E16.28.25.0"),sQuery(id+"F0.wireOp",EDGE,"E16.32.25.0"),sQuery(id+"F0.wireOp",EDGE,"E16.36.25.0"),sQuery(id+"F0.wireOp",EDGE,"E16.40.25.0"),sQuery(id+"F0.wireOp",EDGE,"E16.44.25.0"),sQuery(id+"F0.wireOp",EDGE,"E16.1.26.0"),sQuery(id+"F0.wireOp",EDGE,"E16.6.26.0"),sQuery(id+"F0.wireOp",EDGE,"E16.9.26.0"),sQuery(id+"F0.wireOp",EDGE,"E16.12.26.0"),sQuery(id+"F0.wireOp",EDGE,"E16.18.26.0"),sQuery(id+"F0.wireOp",EDGE,"E16.21.26.0"),sQuery(id+"F0.wireOp",EDGE,"E16.24.26.0"),sQuery(id+"F0.wireOp",EDGE,"E16.28.26.0"),sQuery(id+"F0.wireOp",EDGE,"E16.32.26.0"),sQuery(id+"F0.wireOp",EDGE,"E16.36.26.0"),sQuery(id+"F0.wireOp",EDGE,"E16.40.26.0"),sQuery(id+"F0.wireOp",EDGE,"E16.44.26.0"),sQuery(id+"F0.wireOp",EDGE,"E16.1.27.0"),sQuery(id+"F0.wireOp",EDGE,"E16.6.27.0"),sQuery(id+"F0.wireOp",EDGE,"E16.9.27.0"),sQuery(id+"F0.wireOp",EDGE,"E16.12.27.0"),sQuery(id+"F0.wireOp",EDGE,"E16.18.27.0"),sQuery(id+"F0.wireOp",EDGE,"E16.21.27.0"),sQuery(id+"F0.wireOp",EDGE,"E16.24.27.0"),sQuery(id+"F0.wireOp",EDGE,"E16.28.27.0"),sQuery(id+"F0.wireOp",EDGE,"E16.32.27.0"),sQuery(id+"F0.wireOp",EDGE,"E16.36.27.0"),sQuery(id+"F0.wireOp",EDGE,"E16.40.27.0"),sQuery(id+"F0.wireOp",EDGE,"E16.44.27.0"),sQuery(id+"F0.wireOp",EDGE,"E17.trimOffspring"),sQuery(id+"F0.wireOp",EDGE,"E18.trimOffspring"),sQuery(id+"F0.wireOp",EDGE,"E19.trimOffspring"),sQuery(id+"F0.wireOp",EDGE,"E20.trimOffspring"),sQuery(id+"F0.wireOp",EDGE,"E21.trimOffspring"),sQuery(id+"F0.wireOp",EDGE,"E22.trimOffspring"),sQuery(id+"F0.wireOp",EDGE,"E23.trimOffspring"),sQuery(id+"F0.wireOp",EDGE,"E24.trimOffspring"),sQuery(id+"F0.wireOp",EDGE,"E25.trimOffspring"),sQuery(id+"F0.wireOp",EDGE,"E26.trimOffspring"),sQuery(id+"F0.wireOp",EDGE,"E27.trimOffspring"),sQuery(id+"F0.wireOp",EDGE,"E28.trimOffspring"),sQuery(id+"F0.wireOp",EDGE,"E29.trimOffspring"),sQuery(id+"F0.wireOp",EDGE,"E30.trimOffspring"),sQuery(id+"F0.wireOp",EDGE,"E31.trimOffspring"),sQuery(id+"F0.wireOp",EDGE,"E32.trimOffspring"),sQuery(id+"F0.wireOp",EDGE,"E33.trimOffspring"),sQuery(id+"F0.wireOp",EDGE,"E34.trimOffspring"),sQuery(id+"F0.wireOp",EDGE,"E35.trimOffspring"),sQuery(id+"F0.wireOp",EDGE,"E36.trimOffspring"),sQuery(id+"F0.wireOp",EDGE,"E37.trimOffspring"),sQuery(id+"F0.wireOp",EDGE,"E38.trimOffspring"),sQuery(id+"F0.wireOp",EDGE,"E39.trimOffspring"),sQuery(id+"F0.wireOp",EDGE,"E40.trimOffspring"),sQuery(id+"F0.wireOp",EDGE,"E41.trimOffspring"),sQuery(id+"F0.wireOp",EDGE,"E42.trimOffspring"),sQuery(id+"F0.wireOp",EDGE,"E43.trimOffspring")])],"isStart":false});
            var sketch = newSketch(context, id + "F6", { "sketchPlane" : qUnion([Q0])});
            skLineSegment(sketch, "E46", {"start": v(0, 0) * mm, "end": v(11.43, 0) * mm, "construction": true});
            skCircle(sketch, "E47", {"center": v(11.43, 0) * mm, "radius": 1.59 * mm});
            skSolve(sketch);
        }
        {
            var Q0;
            Q0 = qSketchRegion(id + "F6", true);
            extrude(context, id + "F7", {"entities" : qUnion([Q0]), "operationType" : NewBodyOperationType.ADD, "depth" : 6.35 * mm});
        }
    });
